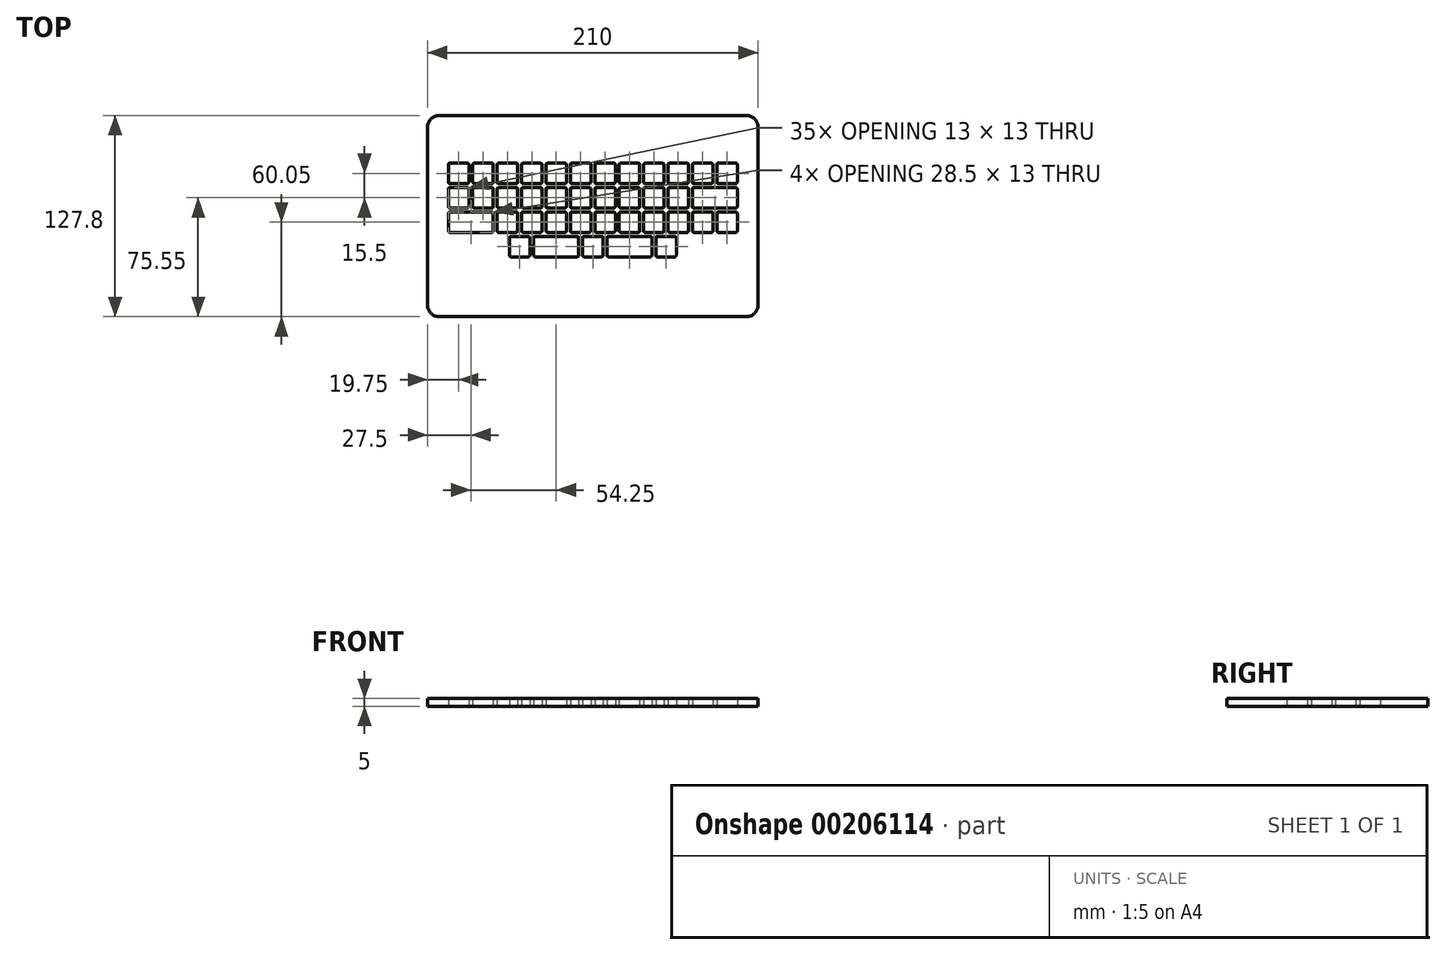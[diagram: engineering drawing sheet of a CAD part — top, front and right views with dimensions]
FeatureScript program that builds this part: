
annotation { "Feature Type Name" : "Feature", "Feature Type Description" : "" }
export const myFeature = defineFeature(function(context is Context, id is Id, definition is map)
    precondition{}
    {
        {
            var Q0;
            Q0=qCreatedBy(makeId("Top.planeOp"),FACE);
            var sketch = newSketch(context, id + "F0", { "sketchPlane" : qUnion([Q0])});
            skLineSegment(sketch, "E0.bottom", {"start": v(1, 0) * mm, "end": v(12, 0) * mm});
            skLineSegment(sketch, "E0.top", {"start": v(1, -13) * mm, "end": v(12, -13) * mm});
            skLineSegment(sketch, "E0.left", {"start": v(0, -1) * mm, "end": v(0, -12) * mm});
            skLineSegment(sketch, "E0.right", {"start": v(13, -1) * mm, "end": v(13, -12) * mm});
            skPoint(sketch, "E1.visualSharp", {"position": v(13, 0) * mm});
            skArc(sketch, "E1.filletArc", {"start": v(13, -1) * mm, "mid": v(12.7, -0.3) * mm, "end": v(12, 0) * mm});
            skArc(sketch, "E2.filletArc", {"start": v(12, -13) * mm, "mid": v(12.7, -12.7) * mm, "end": v(13, -12) * mm});
            skArc(sketch, "E3.filletArc", {"start": v(0, -12) * mm, "mid": v(0.3, -12.7) * mm, "end": v(1, -13) * mm});
            skPoint(sketch, "E4.visualSharp", {"position": v(0, 0) * mm});
            skArc(sketch, "E4.filletArc", {"start": v(1, 0) * mm, "mid": v(0.3, -0.3) * mm, "end": v(0, -1) * mm});
            skLineSegment(sketch, "E5.1.0.1", {"start": v(16.5, -13) * mm, "end": v(27.5, -13) * mm});
            skLineSegment(sketch, "E5.1.0.2", {"start": v(28.5, -1) * mm, "end": v(28.5, -12) * mm});
            skLineSegment(sketch, "E5.1.0.3", {"start": v(15.5, -1) * mm, "end": v(15.5, -12) * mm});
            skLineSegment(sketch, "E5.1.0.4", {"start": v(16.5, 0) * mm, "end": v(27.5, 0) * mm});
            skPoint(sketch, "E5.1.0.5", {"position": v(15.5, 0) * mm});
            skPoint(sketch, "E5.1.0.6", {"position": v(28.5, 0) * mm});
            skArc(sketch, "E5.1.0.8", {"start": v(28.5, -1) * mm, "mid": v(28.2, -0.3) * mm, "end": v(27.5, 0) * mm});
            skArc(sketch, "E5.1.0.9", {"start": v(27.5, -13) * mm, "mid": v(28.2, -12.7) * mm, "end": v(28.5, -12) * mm});
            skArc(sketch, "E5.1.0.10", {"start": v(15.5, -12) * mm, "mid": v(15.8, -12.7) * mm, "end": v(16.5, -13) * mm});
            skArc(sketch, "E5.1.0.11", {"start": v(16.5, 0) * mm, "mid": v(15.8, -0.3) * mm, "end": v(15.5, -1) * mm});
            skLineSegment(sketch, "E5.2.0.1", {"start": v(32, -13) * mm, "end": v(43, -13) * mm});
            skLineSegment(sketch, "E5.2.0.2", {"start": v(44, -1) * mm, "end": v(44, -12) * mm});
            skLineSegment(sketch, "E5.2.0.3", {"start": v(31, -1) * mm, "end": v(31, -12) * mm});
            skLineSegment(sketch, "E5.2.0.4", {"start": v(32, 0) * mm, "end": v(43, 0) * mm});
            skPoint(sketch, "E5.2.0.5", {"position": v(31, 0) * mm});
            skPoint(sketch, "E5.2.0.6", {"position": v(44, 0) * mm});
            skArc(sketch, "E5.2.0.8", {"start": v(44, -1) * mm, "mid": v(43.7, -0.3) * mm, "end": v(43, 0) * mm});
            skArc(sketch, "E5.2.0.9", {"start": v(43, -13) * mm, "mid": v(43.7, -12.7) * mm, "end": v(44, -12) * mm});
            skArc(sketch, "E5.2.0.10", {"start": v(31, -12) * mm, "mid": v(31.3, -12.7) * mm, "end": v(32, -13) * mm});
            skArc(sketch, "E5.2.0.11", {"start": v(32, 0) * mm, "mid": v(31.3, -0.3) * mm, "end": v(31, -1) * mm});
            skLineSegment(sketch, "E5.3.0.1", {"start": v(47.5, -13) * mm, "end": v(58.5, -13) * mm});
            skLineSegment(sketch, "E5.3.0.2", {"start": v(59.5, -1) * mm, "end": v(59.5, -12) * mm});
            skLineSegment(sketch, "E5.3.0.3", {"start": v(46.5, -1) * mm, "end": v(46.5, -12) * mm});
            skLineSegment(sketch, "E5.3.0.4", {"start": v(47.5, 0) * mm, "end": v(58.5, 0) * mm});
            skPoint(sketch, "E5.3.0.5", {"position": v(46.5, 0) * mm});
            skPoint(sketch, "E5.3.0.6", {"position": v(59.5, 0) * mm});
            skArc(sketch, "E5.3.0.8", {"start": v(59.5, -1) * mm, "mid": v(59.2, -0.3) * mm, "end": v(58.5, 0) * mm});
            skArc(sketch, "E5.3.0.9", {"start": v(58.5, -13) * mm, "mid": v(59.2, -12.7) * mm, "end": v(59.5, -12) * mm});
            skArc(sketch, "E5.3.0.10", {"start": v(46.5, -12) * mm, "mid": v(46.8, -12.7) * mm, "end": v(47.5, -13) * mm});
            skArc(sketch, "E5.3.0.11", {"start": v(47.5, 0) * mm, "mid": v(46.8, -0.3) * mm, "end": v(46.5, -1) * mm});
            skLineSegment(sketch, "E5.4.0.1", {"start": v(63, -13) * mm, "end": v(74, -13) * mm});
            skLineSegment(sketch, "E5.4.0.2", {"start": v(75, -1) * mm, "end": v(75, -12) * mm});
            skLineSegment(sketch, "E5.4.0.3", {"start": v(62, -1) * mm, "end": v(62, -12) * mm});
            skLineSegment(sketch, "E5.4.0.4", {"start": v(63, 0) * mm, "end": v(74, 0) * mm});
            skPoint(sketch, "E5.4.0.5", {"position": v(62, 0) * mm});
            skPoint(sketch, "E5.4.0.6", {"position": v(75, 0) * mm});
            skArc(sketch, "E5.4.0.8", {"start": v(75, -1) * mm, "mid": v(74.7, -0.3) * mm, "end": v(74, 0) * mm});
            skArc(sketch, "E5.4.0.9", {"start": v(74, -13) * mm, "mid": v(74.7, -12.7) * mm, "end": v(75, -12) * mm});
            skArc(sketch, "E5.4.0.10", {"start": v(62, -12) * mm, "mid": v(62.3, -12.7) * mm, "end": v(63, -13) * mm});
            skArc(sketch, "E5.4.0.11", {"start": v(63, 0) * mm, "mid": v(62.3, -0.3) * mm, "end": v(62, -1) * mm});
            skLineSegment(sketch, "E5.5.0.1", {"start": v(78.5, -13) * mm, "end": v(89.5, -13) * mm});
            skLineSegment(sketch, "E5.5.0.2", {"start": v(90.5, -1) * mm, "end": v(90.5, -12) * mm});
            skLineSegment(sketch, "E5.5.0.3", {"start": v(77.5, -1) * mm, "end": v(77.5, -12) * mm});
            skLineSegment(sketch, "E5.5.0.4", {"start": v(78.5, 0) * mm, "end": v(89.5, 0) * mm});
            skPoint(sketch, "E5.5.0.5", {"position": v(77.5, 0) * mm});
            skPoint(sketch, "E5.5.0.6", {"position": v(90.5, 0) * mm});
            skArc(sketch, "E5.5.0.8", {"start": v(90.5, -1) * mm, "mid": v(90.2, -0.3) * mm, "end": v(89.5, 0) * mm});
            skArc(sketch, "E5.5.0.9", {"start": v(89.5, -13) * mm, "mid": v(90.2, -12.7) * mm, "end": v(90.5, -12) * mm});
            skArc(sketch, "E5.5.0.10", {"start": v(77.5, -12) * mm, "mid": v(77.8, -12.7) * mm, "end": v(78.5, -13) * mm});
            skArc(sketch, "E5.5.0.11", {"start": v(78.5, 0) * mm, "mid": v(77.8, -0.3) * mm, "end": v(77.5, -1) * mm});
            skLineSegment(sketch, "E5.6.0.1", {"start": v(94, -13) * mm, "end": v(105, -13) * mm});
            skLineSegment(sketch, "E5.6.0.2", {"start": v(106, -1) * mm, "end": v(106, -12) * mm});
            skLineSegment(sketch, "E5.6.0.3", {"start": v(93, -1) * mm, "end": v(93, -12) * mm});
            skLineSegment(sketch, "E5.6.0.4", {"start": v(94, 0) * mm, "end": v(105, 0) * mm});
            skPoint(sketch, "E5.6.0.5", {"position": v(93, 0) * mm});
            skPoint(sketch, "E5.6.0.6", {"position": v(106, 0) * mm});
            skArc(sketch, "E5.6.0.8", {"start": v(106, -1) * mm, "mid": v(105.7, -0.3) * mm, "end": v(105, 0) * mm});
            skArc(sketch, "E5.6.0.9", {"start": v(105, -13) * mm, "mid": v(105.7, -12.7) * mm, "end": v(106, -12) * mm});
            skArc(sketch, "E5.6.0.10", {"start": v(93, -12) * mm, "mid": v(93.3, -12.7) * mm, "end": v(94, -13) * mm});
            skArc(sketch, "E5.6.0.11", {"start": v(94, 0) * mm, "mid": v(93.3, -0.3) * mm, "end": v(93, -1) * mm});
            skLineSegment(sketch, "E5.7.0.1", {"start": v(109.5, -13) * mm, "end": v(120.5, -13) * mm});
            skLineSegment(sketch, "E5.7.0.2", {"start": v(121.5, -1) * mm, "end": v(121.5, -12) * mm});
            skLineSegment(sketch, "E5.7.0.3", {"start": v(108.5, -1) * mm, "end": v(108.5, -12) * mm});
            skLineSegment(sketch, "E5.7.0.4", {"start": v(109.5, 0) * mm, "end": v(120.5, 0) * mm});
            skPoint(sketch, "E5.7.0.5", {"position": v(108.5, 0) * mm});
            skPoint(sketch, "E5.7.0.6", {"position": v(121.5, 0) * mm});
            skArc(sketch, "E5.7.0.8", {"start": v(121.5, -1) * mm, "mid": v(121.2, -0.3) * mm, "end": v(120.5, 0) * mm});
            skArc(sketch, "E5.7.0.9", {"start": v(120.5, -13) * mm, "mid": v(121.2, -12.7) * mm, "end": v(121.5, -12) * mm});
            skArc(sketch, "E5.7.0.10", {"start": v(108.5, -12) * mm, "mid": v(108.8, -12.7) * mm, "end": v(109.5, -13) * mm});
            skArc(sketch, "E5.7.0.11", {"start": v(109.5, 0) * mm, "mid": v(108.8, -0.3) * mm, "end": v(108.5, -1) * mm});
            skLineSegment(sketch, "E5.8.0.1", {"start": v(125, -13) * mm, "end": v(136, -13) * mm});
            skLineSegment(sketch, "E5.8.0.2", {"start": v(137, -1) * mm, "end": v(137, -12) * mm});
            skLineSegment(sketch, "E5.8.0.3", {"start": v(124, -1) * mm, "end": v(124, -12) * mm});
            skLineSegment(sketch, "E5.8.0.4", {"start": v(125, 0) * mm, "end": v(136, 0) * mm});
            skPoint(sketch, "E5.8.0.5", {"position": v(124, 0) * mm});
            skPoint(sketch, "E5.8.0.6", {"position": v(137, 0) * mm});
            skArc(sketch, "E5.8.0.8", {"start": v(137, -1) * mm, "mid": v(136.7, -0.3) * mm, "end": v(136, 0) * mm});
            skArc(sketch, "E5.8.0.9", {"start": v(136, -13) * mm, "mid": v(136.7, -12.7) * mm, "end": v(137, -12) * mm});
            skArc(sketch, "E5.8.0.10", {"start": v(124, -12) * mm, "mid": v(124.3, -12.7) * mm, "end": v(125, -13) * mm});
            skArc(sketch, "E5.8.0.11", {"start": v(125, 0) * mm, "mid": v(124.3, -0.3) * mm, "end": v(124, -1) * mm});
            skLineSegment(sketch, "E5.9.0.1", {"start": v(140.5, -13) * mm, "end": v(151.5, -13) * mm});
            skLineSegment(sketch, "E5.9.0.2", {"start": v(152.5, -1) * mm, "end": v(152.5, -12) * mm});
            skLineSegment(sketch, "E5.9.0.3", {"start": v(139.5, -1) * mm, "end": v(139.5, -12) * mm});
            skLineSegment(sketch, "E5.9.0.4", {"start": v(140.5, 0) * mm, "end": v(151.5, 0) * mm});
            skPoint(sketch, "E5.9.0.5", {"position": v(139.5, 0) * mm});
            skPoint(sketch, "E5.9.0.6", {"position": v(152.5, 0) * mm});
            skArc(sketch, "E5.9.0.8", {"start": v(152.5, -1) * mm, "mid": v(152.2, -0.3) * mm, "end": v(151.5, 0) * mm});
            skArc(sketch, "E5.9.0.9", {"start": v(151.5, -13) * mm, "mid": v(152.2, -12.7) * mm, "end": v(152.5, -12) * mm});
            skArc(sketch, "E5.9.0.10", {"start": v(139.5, -12) * mm, "mid": v(139.8, -12.7) * mm, "end": v(140.5, -13) * mm});
            skArc(sketch, "E5.9.0.11", {"start": v(140.5, 0) * mm, "mid": v(139.8, -0.3) * mm, "end": v(139.5, -1) * mm});
            skLineSegment(sketch, "E5.10.0.1", {"start": v(156, -13) * mm, "end": v(167, -13) * mm});
            skLineSegment(sketch, "E5.10.0.2", {"start": v(168, -1) * mm, "end": v(168, -12) * mm});
            skLineSegment(sketch, "E5.10.0.3", {"start": v(155, -1) * mm, "end": v(155, -12) * mm});
            skLineSegment(sketch, "E5.10.0.4", {"start": v(156, 0) * mm, "end": v(167, 0) * mm});
            skPoint(sketch, "E5.10.0.5", {"position": v(155, 0) * mm});
            skPoint(sketch, "E5.10.0.6", {"position": v(168, 0) * mm});
            skArc(sketch, "E5.10.0.8", {"start": v(168, -1) * mm, "mid": v(167.7, -0.3) * mm, "end": v(167, 0) * mm});
            skArc(sketch, "E5.10.0.9", {"start": v(167, -13) * mm, "mid": v(167.7, -12.7) * mm, "end": v(168, -12) * mm});
            skArc(sketch, "E5.10.0.10", {"start": v(155, -12) * mm, "mid": v(155.3, -12.7) * mm, "end": v(156, -13) * mm});
            skArc(sketch, "E5.10.0.11", {"start": v(156, 0) * mm, "mid": v(155.3, -0.3) * mm, "end": v(155, -1) * mm});
            skLineSegment(sketch, "E5.11.0.1", {"start": v(171.5, -13) * mm, "end": v(182.5, -13) * mm});
            skLineSegment(sketch, "E5.11.0.2", {"start": v(183.5, -1) * mm, "end": v(183.5, -12) * mm});
            skLineSegment(sketch, "E5.11.0.3", {"start": v(170.5, -1) * mm, "end": v(170.5, -12) * mm});
            skLineSegment(sketch, "E5.11.0.4", {"start": v(171.5, 0) * mm, "end": v(182.5, 0) * mm});
            skPoint(sketch, "E5.11.0.5", {"position": v(170.5, 0) * mm});
            skPoint(sketch, "E5.11.0.6", {"position": v(183.5, 0) * mm});
            skArc(sketch, "E5.11.0.8", {"start": v(183.5, -1) * mm, "mid": v(183.2, -0.3) * mm, "end": v(182.5, 0) * mm});
            skArc(sketch, "E5.11.0.9", {"start": v(182.5, -13) * mm, "mid": v(183.2, -12.7) * mm, "end": v(183.5, -12) * mm});
            skArc(sketch, "E5.11.0.10", {"start": v(170.5, -12) * mm, "mid": v(170.8, -12.7) * mm, "end": v(171.5, -13) * mm});
            skArc(sketch, "E5.11.0.11", {"start": v(171.5, 0) * mm, "mid": v(170.8, -0.3) * mm, "end": v(170.5, -1) * mm});
            skLineSegment(sketch, "E5.direction1", {"start": v(0, -13) * mm, "end": v(15.5, -13) * mm, "construction": true});
            skLineSegment(sketch, "E6.0.1.0", {"start": v(121.5, -16.5) * mm, "end": v(121.5, -27.5) * mm});
            skPoint(sketch, "E6.0.1.1", {"position": v(183.5, -15.5) * mm});
            skPoint(sketch, "E6.0.1.2", {"position": v(155, -15.5) * mm});
            skLineSegment(sketch, "E6.0.1.3", {"start": v(140.5, -15.5) * mm, "end": v(151.5, -15.5) * mm});
            skLineSegment(sketch, "E6.0.1.5", {"start": v(47.5, -15.5) * mm, "end": v(58.5, -15.5) * mm});
            skLineSegment(sketch, "E6.0.1.6", {"start": v(78.5, -15.5) * mm, "end": v(89.5, -15.5) * mm});
            skLineSegment(sketch, "E6.0.1.7", {"start": v(109.5, -15.5) * mm, "end": v(120.5, -15.5) * mm});
            skPoint(sketch, "E6.0.1.8", {"position": v(46.5, -15.5) * mm});
            skLineSegment(sketch, "E6.0.1.9", {"start": v(63, -15.5) * mm, "end": v(74, -15.5) * mm});
            skLineSegment(sketch, "E6.0.1.10", {"start": v(94, -15.5) * mm, "end": v(105, -15.5) * mm});
            skLineSegment(sketch, "E6.0.1.11", {"start": v(125, -15.5) * mm, "end": v(136, -15.5) * mm});
            skLineSegment(sketch, "E6.0.1.13", {"start": v(46.5, -16.5) * mm, "end": v(46.5, -27.5) * mm});
            skLineSegment(sketch, "E6.0.1.14", {"start": v(108.5, -16.5) * mm, "end": v(108.5, -27.5) * mm});
            skPoint(sketch, "E6.0.1.15", {"position": v(137, -15.5) * mm});
            skPoint(sketch, "E6.0.1.16", {"position": v(13, -15.5) * mm});
            skLineSegment(sketch, "E6.0.1.17", {"start": v(75, -16.5) * mm, "end": v(75, -27.5) * mm});
            skLineSegment(sketch, "E6.0.1.19", {"start": v(155, -16.5) * mm, "end": v(155, -27.5) * mm});
            skLineSegment(sketch, "E6.0.1.20", {"start": v(31, -16.5) * mm, "end": v(31, -27.5) * mm});
            skPoint(sketch, "E6.0.1.21", {"position": v(124, -15.5) * mm});
            skLineSegment(sketch, "E6.0.1.22", {"start": v(152.5, -16.5) * mm, "end": v(152.5, -27.5) * mm});
            skPoint(sketch, "E6.0.1.23", {"position": v(0, -15.5) * mm});
            skLineSegment(sketch, "E6.0.1.24", {"start": v(44, -16.5) * mm, "end": v(44, -27.5) * mm});
            skLineSegment(sketch, "E6.0.1.25", {"start": v(59.5, -16.5) * mm, "end": v(59.5, -27.5) * mm});
            skPoint(sketch, "E6.0.1.26", {"position": v(31, -15.5) * mm});
            skPoint(sketch, "E6.0.1.27", {"position": v(90.5, -15.5) * mm});
            skLineSegment(sketch, "E6.0.1.28", {"start": v(171.5, -28.5) * mm, "end": v(182.5, -28.5) * mm});
            skLineSegment(sketch, "E6.0.1.29", {"start": v(109.5, -28.5) * mm, "end": v(120.5, -28.5) * mm});
            skLineSegment(sketch, "E6.0.1.30", {"start": v(78.5, -28.5) * mm, "end": v(89.5, -28.5) * mm});
            skPoint(sketch, "E6.0.1.31", {"position": v(139.5, -15.5) * mm});
            skPoint(sketch, "E6.0.1.32", {"position": v(15.5, -15.5) * mm});
            skLineSegment(sketch, "E6.0.1.33", {"start": v(125, -28.5) * mm, "end": v(136, -28.5) * mm});
            skLineSegment(sketch, "E6.0.1.34", {"start": v(94, -28.5) * mm, "end": v(105, -28.5) * mm});
            skLineSegment(sketch, "E6.0.1.35", {"start": v(156, -28.5) * mm, "end": v(167, -28.5) * mm});
            skLineSegment(sketch, "E6.0.1.36", {"start": v(32, -28.5) * mm, "end": v(43, -28.5) * mm});
            skPoint(sketch, "E6.0.1.37", {"position": v(77.5, -15.5) * mm});
            skLineSegment(sketch, "E6.0.1.38", {"start": v(0, -28.5) * mm, "end": v(15.5, -28.5) * mm, "construction": true});
            skLineSegment(sketch, "E6.0.1.39", {"start": v(16.5, -15.5) * mm, "end": v(27.5, -15.5) * mm});
            skLineSegment(sketch, "E6.0.1.40", {"start": v(15.5, -16.5) * mm, "end": v(15.5, -27.5) * mm});
            skLineSegment(sketch, "E6.0.1.41", {"start": v(28.5, -16.5) * mm, "end": v(28.5, -27.5) * mm});
            skLineSegment(sketch, "E6.0.1.42", {"start": v(16.5, -28.5) * mm, "end": v(27.5, -28.5) * mm});
            skLineSegment(sketch, "E6.0.1.43", {"start": v(13, -16.5) * mm, "end": v(13, -27.5) * mm});
            skLineSegment(sketch, "E6.0.1.44", {"start": v(0, -16.5) * mm, "end": v(0, -27.5) * mm});
            skPoint(sketch, "E6.0.1.45", {"position": v(44, -15.5) * mm});
            skLineSegment(sketch, "E6.0.1.46", {"start": v(77.5, -16.5) * mm, "end": v(77.5, -27.5) * mm});
            skPoint(sketch, "E6.0.1.47", {"position": v(108.5, -15.5) * mm});
            skPoint(sketch, "E6.0.1.48", {"position": v(168, -15.5) * mm});
            skPoint(sketch, "E6.0.1.49", {"position": v(93, -15.5) * mm});
            skPoint(sketch, "E6.0.1.50", {"position": v(59.5, -15.5) * mm});
            skPoint(sketch, "E6.0.1.51", {"position": v(75, -15.5) * mm});
            skPoint(sketch, "E6.0.1.52", {"position": v(121.5, -15.5) * mm});
            skPoint(sketch, "E6.0.1.53", {"position": v(170.5, -15.5) * mm});
            skPoint(sketch, "E6.0.1.54", {"position": v(62, -15.5) * mm});
            skLineSegment(sketch, "E6.0.1.55", {"start": v(139.5, -16.5) * mm, "end": v(139.5, -27.5) * mm});
            skPoint(sketch, "E6.0.1.56", {"position": v(106, -15.5) * mm});
            skLineSegment(sketch, "E6.0.1.57", {"start": v(32, -15.5) * mm, "end": v(43, -15.5) * mm});
            skLineSegment(sketch, "E6.0.1.58", {"start": v(63, -28.5) * mm, "end": v(74, -28.5) * mm});
            skLineSegment(sketch, "E6.0.1.59", {"start": v(47.5, -28.5) * mm, "end": v(58.5, -28.5) * mm});
            skLineSegment(sketch, "E6.0.1.60", {"start": v(140.5, -28.5) * mm, "end": v(151.5, -28.5) * mm});
            skLineSegment(sketch, "E6.0.1.61", {"start": v(137, -16.5) * mm, "end": v(137, -27.5) * mm});
            skLineSegment(sketch, "E6.0.1.62", {"start": v(106, -16.5) * mm, "end": v(106, -27.5) * mm});
            skPoint(sketch, "E6.0.1.64", {"position": v(152.5, -15.5) * mm});
            skLineSegment(sketch, "E6.0.1.65", {"start": v(90.5, -16.5) * mm, "end": v(90.5, -27.5) * mm});
            skLineSegment(sketch, "E6.0.1.66", {"start": v(183.5, -16.5) * mm, "end": v(183.5, -27.5) * mm});
            skLineSegment(sketch, "E6.0.1.67", {"start": v(124, -16.5) * mm, "end": v(124, -27.5) * mm});
            skLineSegment(sketch, "E6.0.1.68", {"start": v(93, -16.5) * mm, "end": v(93, -27.5) * mm});
            skLineSegment(sketch, "E6.0.1.69", {"start": v(62, -16.5) * mm, "end": v(62, -27.5) * mm});
            skPoint(sketch, "E6.0.1.70", {"position": v(28.5, -15.5) * mm});
            skLineSegment(sketch, "E6.0.1.71", {"start": v(1, -15.5) * mm, "end": v(12, -15.5) * mm});
            skLineSegment(sketch, "E6.0.1.72", {"start": v(1, -28.5) * mm, "end": v(12, -28.5) * mm});
            skArc(sketch, "E6.0.1.73", {"start": v(182.5, -28.5) * mm, "mid": v(183.2, -28.2) * mm, "end": v(183.5, -27.5) * mm});
            skArc(sketch, "E6.0.1.74", {"start": v(89.5, -28.5) * mm, "mid": v(90.2, -28.2) * mm, "end": v(90.5, -27.5) * mm});
            skArc(sketch, "E6.0.1.75", {"start": v(31, -27.5) * mm, "mid": v(31.3, -28.2) * mm, "end": v(32, -28.5) * mm});
            skArc(sketch, "E6.0.1.76", {"start": v(74, -28.5) * mm, "mid": v(74.7, -28.2) * mm, "end": v(75, -27.5) * mm});
            skArc(sketch, "E6.0.1.77", {"start": v(155, -27.5) * mm, "mid": v(155.3, -28.2) * mm, "end": v(156, -28.5) * mm});
            skArc(sketch, "E6.0.1.78", {"start": v(77.5, -27.5) * mm, "mid": v(77.8, -28.2) * mm, "end": v(78.5, -28.5) * mm});
            skArc(sketch, "E6.0.1.79", {"start": v(139.5, -27.5) * mm, "mid": v(139.8, -28.2) * mm, "end": v(140.5, -28.5) * mm});
            skArc(sketch, "E6.0.1.80", {"start": v(93, -27.5) * mm, "mid": v(93.3, -28.2) * mm, "end": v(94, -28.5) * mm});
            skArc(sketch, "E6.0.1.81", {"start": v(62, -27.5) * mm, "mid": v(62.3, -28.2) * mm, "end": v(63, -28.5) * mm});
            skArc(sketch, "E6.0.1.82", {"start": v(75, -16.5) * mm, "mid": v(74.7, -15.8) * mm, "end": v(74, -15.5) * mm});
            skArc(sketch, "E6.0.1.83", {"start": v(44, -16.5) * mm, "mid": v(43.7, -15.8) * mm, "end": v(43, -15.5) * mm});
            skArc(sketch, "E6.0.1.84", {"start": v(32, -15.5) * mm, "mid": v(31.3, -15.8) * mm, "end": v(31, -16.5) * mm});
            skArc(sketch, "E6.0.1.85", {"start": v(1, -15.5) * mm, "mid": v(0.3, -15.8) * mm, "end": v(0, -16.5) * mm});
            skArc(sketch, "E6.0.1.86", {"start": v(0, -27.5) * mm, "mid": v(0.3, -28.2) * mm, "end": v(1, -28.5) * mm});
            skArc(sketch, "E6.0.1.87", {"start": v(12, -28.5) * mm, "mid": v(12.7, -28.2) * mm, "end": v(13, -27.5) * mm});
            skArc(sketch, "E6.0.1.88", {"start": v(13, -16.5) * mm, "mid": v(12.7, -15.8) * mm, "end": v(12, -15.5) * mm});
            skArc(sketch, "E6.0.1.89", {"start": v(27.5, -28.5) * mm, "mid": v(28.2, -28.2) * mm, "end": v(28.5, -27.5) * mm});
            skArc(sketch, "E6.0.1.90", {"start": v(140.5, -15.5) * mm, "mid": v(139.8, -15.8) * mm, "end": v(139.5, -16.5) * mm});
            skArc(sketch, "E6.0.1.92", {"start": v(46.5, -27.5) * mm, "mid": v(46.8, -28.2) * mm, "end": v(47.5, -28.5) * mm});
            skArc(sketch, "E6.0.1.93", {"start": v(105, -28.5) * mm, "mid": v(105.7, -28.2) * mm, "end": v(106, -27.5) * mm});
            skArc(sketch, "E6.0.1.94", {"start": v(108.5, -27.5) * mm, "mid": v(108.8, -28.2) * mm, "end": v(109.5, -28.5) * mm});
            skArc(sketch, "E6.0.1.95", {"start": v(136, -28.5) * mm, "mid": v(136.7, -28.2) * mm, "end": v(137, -27.5) * mm});
            skArc(sketch, "E6.0.1.97", {"start": v(124, -27.5) * mm, "mid": v(124.3, -28.2) * mm, "end": v(125, -28.5) * mm});
            skArc(sketch, "E6.0.1.98", {"start": v(43, -28.5) * mm, "mid": v(43.7, -28.2) * mm, "end": v(44, -27.5) * mm});
            skArc(sketch, "E6.0.1.99", {"start": v(152.5, -16.5) * mm, "mid": v(152.2, -15.8) * mm, "end": v(151.5, -15.5) * mm});
            skArc(sketch, "E6.0.1.100", {"start": v(183.5, -16.5) * mm, "mid": v(183.2, -15.8) * mm, "end": v(182.5, -15.5) * mm});
            skArc(sketch, "E6.0.1.101", {"start": v(59.5, -16.5) * mm, "mid": v(59.2, -15.8) * mm, "end": v(58.5, -15.5) * mm});
            skArc(sketch, "E6.0.1.102", {"start": v(90.5, -16.5) * mm, "mid": v(90.2, -15.8) * mm, "end": v(89.5, -15.5) * mm});
            skArc(sketch, "E6.0.1.103", {"start": v(121.5, -16.5) * mm, "mid": v(121.2, -15.8) * mm, "end": v(120.5, -15.5) * mm});
            skArc(sketch, "E6.0.1.104", {"start": v(58.5, -28.5) * mm, "mid": v(59.2, -28.2) * mm, "end": v(59.5, -27.5) * mm});
            skArc(sketch, "E6.0.1.105", {"start": v(106, -16.5) * mm, "mid": v(105.7, -15.8) * mm, "end": v(105, -15.5) * mm});
            skArc(sketch, "E6.0.1.106", {"start": v(120.5, -28.5) * mm, "mid": v(121.2, -28.2) * mm, "end": v(121.5, -27.5) * mm});
            skArc(sketch, "E6.0.1.107", {"start": v(137, -16.5) * mm, "mid": v(136.7, -15.8) * mm, "end": v(136, -15.5) * mm});
            skArc(sketch, "E6.0.1.108", {"start": v(151.5, -28.5) * mm, "mid": v(152.2, -28.2) * mm, "end": v(152.5, -27.5) * mm});
            skArc(sketch, "E6.0.1.110", {"start": v(78.5, -15.5) * mm, "mid": v(77.8, -15.8) * mm, "end": v(77.5, -16.5) * mm});
            skArc(sketch, "E6.0.1.111", {"start": v(15.5, -27.5) * mm, "mid": v(15.8, -28.2) * mm, "end": v(16.5, -28.5) * mm});
            skArc(sketch, "E6.0.1.112", {"start": v(16.5, -15.5) * mm, "mid": v(15.8, -15.8) * mm, "end": v(15.5, -16.5) * mm});
            skArc(sketch, "E6.0.1.113", {"start": v(28.5, -16.5) * mm, "mid": v(28.2, -15.8) * mm, "end": v(27.5, -15.5) * mm});
            skArc(sketch, "E6.0.1.114", {"start": v(94, -15.5) * mm, "mid": v(93.3, -15.8) * mm, "end": v(93, -16.5) * mm});
            skArc(sketch, "E6.0.1.115", {"start": v(156, -15.5) * mm, "mid": v(155.3, -15.8) * mm, "end": v(155, -16.5) * mm});
            skArc(sketch, "E6.0.1.117", {"start": v(47.5, -15.5) * mm, "mid": v(46.8, -15.8) * mm, "end": v(46.5, -16.5) * mm});
            skArc(sketch, "E6.0.1.118", {"start": v(109.5, -15.5) * mm, "mid": v(108.8, -15.8) * mm, "end": v(108.5, -16.5) * mm});
            skArc(sketch, "E6.0.1.119", {"start": v(63, -15.5) * mm, "mid": v(62.3, -15.8) * mm, "end": v(62, -16.5) * mm});
            skArc(sketch, "E6.0.1.120", {"start": v(125, -15.5) * mm, "mid": v(124.3, -15.8) * mm, "end": v(124, -16.5) * mm});
            skLineSegment(sketch, "E6.0.2.0", {"start": v(121.5, -32) * mm, "end": v(121.5, -43) * mm});
            skPoint(sketch, "E6.0.2.1", {"position": v(183.5, -31) * mm});
            skPoint(sketch, "E6.0.2.2", {"position": v(155, -31) * mm});
            skLineSegment(sketch, "E6.0.2.3", {"start": v(140.5, -31) * mm, "end": v(151.5, -31) * mm});
            skLineSegment(sketch, "E6.0.2.4", {"start": v(171.5, -31) * mm, "end": v(182.5, -31) * mm});
            skLineSegment(sketch, "E6.0.2.5", {"start": v(47.5, -31) * mm, "end": v(58.5, -31) * mm});
            skLineSegment(sketch, "E6.0.2.6", {"start": v(78.5, -31) * mm, "end": v(89.5, -31) * mm});
            skLineSegment(sketch, "E6.0.2.7", {"start": v(109.5, -31) * mm, "end": v(120.5, -31) * mm});
            skPoint(sketch, "E6.0.2.8", {"position": v(46.5, -31) * mm});
            skLineSegment(sketch, "E6.0.2.9", {"start": v(63, -31) * mm, "end": v(74, -31) * mm});
            skLineSegment(sketch, "E6.0.2.10", {"start": v(94, -31) * mm, "end": v(105, -31) * mm});
            skLineSegment(sketch, "E6.0.2.11", {"start": v(125, -31) * mm, "end": v(136, -31) * mm});
            skLineSegment(sketch, "E6.0.2.12", {"start": v(170.5, -32) * mm, "end": v(170.5, -43) * mm});
            skLineSegment(sketch, "E6.0.2.13", {"start": v(46.5, -32) * mm, "end": v(46.5, -43) * mm});
            skLineSegment(sketch, "E6.0.2.14", {"start": v(108.5, -32) * mm, "end": v(108.5, -43) * mm});
            skPoint(sketch, "E6.0.2.15", {"position": v(137, -31) * mm});
            skPoint(sketch, "E6.0.2.16", {"position": v(13, -31) * mm});
            skLineSegment(sketch, "E6.0.2.17", {"start": v(75, -32) * mm, "end": v(75, -43) * mm});
            skLineSegment(sketch, "E6.0.2.18", {"start": v(168, -32) * mm, "end": v(168, -43) * mm});
            skLineSegment(sketch, "E6.0.2.19", {"start": v(155, -32) * mm, "end": v(155, -43) * mm});
            skLineSegment(sketch, "E6.0.2.20", {"start": v(31, -32) * mm, "end": v(31, -43) * mm});
            skPoint(sketch, "E6.0.2.21", {"position": v(124, -31) * mm});
            skLineSegment(sketch, "E6.0.2.22", {"start": v(152.5, -32) * mm, "end": v(152.5, -43) * mm});
            skPoint(sketch, "E6.0.2.23", {"position": v(0, -31) * mm});
            skLineSegment(sketch, "E6.0.2.24", {"start": v(44, -32) * mm, "end": v(44, -43) * mm});
            skLineSegment(sketch, "E6.0.2.25", {"start": v(59.5, -32) * mm, "end": v(59.5, -43) * mm});
            skPoint(sketch, "E6.0.2.26", {"position": v(31, -31) * mm});
            skPoint(sketch, "E6.0.2.27", {"position": v(90.5, -31) * mm});
            skLineSegment(sketch, "E6.0.2.28", {"start": v(171.5, -44) * mm, "end": v(182.5, -44) * mm});
            skLineSegment(sketch, "E6.0.2.29", {"start": v(109.5, -44) * mm, "end": v(120.5, -44) * mm});
            skLineSegment(sketch, "E6.0.2.30", {"start": v(78.5, -44) * mm, "end": v(89.5, -44) * mm});
            skPoint(sketch, "E6.0.2.31", {"position": v(139.5, -31) * mm});
            skPoint(sketch, "E6.0.2.32", {"position": v(15.5, -31) * mm});
            skLineSegment(sketch, "E6.0.2.33", {"start": v(125, -44) * mm, "end": v(136, -44) * mm});
            skLineSegment(sketch, "E6.0.2.34", {"start": v(94, -44) * mm, "end": v(105, -44) * mm});
            skLineSegment(sketch, "E6.0.2.35", {"start": v(156, -44) * mm, "end": v(167, -44) * mm});
            skLineSegment(sketch, "E6.0.2.36", {"start": v(32, -44) * mm, "end": v(43, -44) * mm});
            skPoint(sketch, "E6.0.2.37", {"position": v(77.5, -31) * mm});
            skLineSegment(sketch, "E6.0.2.38", {"start": v(0, -44) * mm, "end": v(15.5, -44) * mm, "construction": true});
            skLineSegment(sketch, "E6.0.2.39", {"start": v(16.5, -31) * mm, "end": v(27.5, -31) * mm});
            skLineSegment(sketch, "E6.0.2.41", {"start": v(28.5, -32) * mm, "end": v(28.5, -43) * mm});
            skLineSegment(sketch, "E6.0.2.42", {"start": v(16.5, -44) * mm, "end": v(27.5, -44) * mm});
            skLineSegment(sketch, "E6.0.2.44", {"start": v(0, -32) * mm, "end": v(0, -43) * mm});
            skPoint(sketch, "E6.0.2.45", {"position": v(44, -31) * mm});
            skLineSegment(sketch, "E6.0.2.46", {"start": v(77.5, -32) * mm, "end": v(77.5, -43) * mm});
            skPoint(sketch, "E6.0.2.47", {"position": v(108.5, -31) * mm});
            skPoint(sketch, "E6.0.2.48", {"position": v(168, -31) * mm});
            skPoint(sketch, "E6.0.2.49", {"position": v(93, -31) * mm});
            skPoint(sketch, "E6.0.2.50", {"position": v(59.5, -31) * mm});
            skPoint(sketch, "E6.0.2.51", {"position": v(75, -31) * mm});
            skPoint(sketch, "E6.0.2.52", {"position": v(121.5, -31) * mm});
            skPoint(sketch, "E6.0.2.53", {"position": v(170.5, -31) * mm});
            skPoint(sketch, "E6.0.2.54", {"position": v(62, -31) * mm});
            skLineSegment(sketch, "E6.0.2.55", {"start": v(139.5, -32) * mm, "end": v(139.5, -43) * mm});
            skPoint(sketch, "E6.0.2.56", {"position": v(106, -31) * mm});
            skLineSegment(sketch, "E6.0.2.57", {"start": v(32, -31) * mm, "end": v(43, -31) * mm});
            skLineSegment(sketch, "E6.0.2.58", {"start": v(63, -44) * mm, "end": v(74, -44) * mm});
            skLineSegment(sketch, "E6.0.2.59", {"start": v(47.5, -44) * mm, "end": v(58.5, -44) * mm});
            skLineSegment(sketch, "E6.0.2.60", {"start": v(140.5, -44) * mm, "end": v(151.5, -44) * mm});
            skLineSegment(sketch, "E6.0.2.61", {"start": v(137, -32) * mm, "end": v(137, -43) * mm});
            skLineSegment(sketch, "E6.0.2.62", {"start": v(106, -32) * mm, "end": v(106, -43) * mm});
            skLineSegment(sketch, "E6.0.2.63", {"start": v(156, -31) * mm, "end": v(167, -31) * mm});
            skPoint(sketch, "E6.0.2.64", {"position": v(152.5, -31) * mm});
            skLineSegment(sketch, "E6.0.2.65", {"start": v(90.5, -32) * mm, "end": v(90.5, -43) * mm});
            skLineSegment(sketch, "E6.0.2.66", {"start": v(183.5, -32) * mm, "end": v(183.5, -43) * mm});
            skLineSegment(sketch, "E6.0.2.67", {"start": v(124, -32) * mm, "end": v(124, -43) * mm});
            skLineSegment(sketch, "E6.0.2.68", {"start": v(93, -32) * mm, "end": v(93, -43) * mm});
            skLineSegment(sketch, "E6.0.2.69", {"start": v(62, -32) * mm, "end": v(62, -43) * mm});
            skPoint(sketch, "E6.0.2.70", {"position": v(28.5, -31) * mm});
            skLineSegment(sketch, "E6.0.2.71", {"start": v(1, -31) * mm, "end": v(12, -31) * mm});
            skLineSegment(sketch, "E6.0.2.72", {"start": v(1, -44) * mm, "end": v(12, -44) * mm});
            skArc(sketch, "E6.0.2.73", {"start": v(182.5, -44) * mm, "mid": v(183.2, -43.7) * mm, "end": v(183.5, -43) * mm});
            skArc(sketch, "E6.0.2.74", {"start": v(89.5, -44) * mm, "mid": v(90.2, -43.7) * mm, "end": v(90.5, -43) * mm});
            skArc(sketch, "E6.0.2.75", {"start": v(31, -43) * mm, "mid": v(31.3, -43.7) * mm, "end": v(32, -44) * mm});
            skArc(sketch, "E6.0.2.76", {"start": v(74, -44) * mm, "mid": v(74.7, -43.7) * mm, "end": v(75, -43) * mm});
            skArc(sketch, "E6.0.2.77", {"start": v(155, -43) * mm, "mid": v(155.3, -43.7) * mm, "end": v(156, -44) * mm});
            skArc(sketch, "E6.0.2.78", {"start": v(77.5, -43) * mm, "mid": v(77.8, -43.7) * mm, "end": v(78.5, -44) * mm});
            skArc(sketch, "E6.0.2.79", {"start": v(139.5, -43) * mm, "mid": v(139.8, -43.7) * mm, "end": v(140.5, -44) * mm});
            skArc(sketch, "E6.0.2.80", {"start": v(93, -43) * mm, "mid": v(93.3, -43.7) * mm, "end": v(94, -44) * mm});
            skArc(sketch, "E6.0.2.81", {"start": v(62, -43) * mm, "mid": v(62.3, -43.7) * mm, "end": v(63, -44) * mm});
            skArc(sketch, "E6.0.2.82", {"start": v(75, -32) * mm, "mid": v(74.7, -31.3) * mm, "end": v(74, -31) * mm});
            skArc(sketch, "E6.0.2.83", {"start": v(44, -32) * mm, "mid": v(43.7, -31.3) * mm, "end": v(43, -31) * mm});
            skArc(sketch, "E6.0.2.84", {"start": v(32, -31) * mm, "mid": v(31.3, -31.3) * mm, "end": v(31, -32) * mm});
            skArc(sketch, "E6.0.2.85", {"start": v(1, -31) * mm, "mid": v(0.3, -31.3) * mm, "end": v(0, -32) * mm});
            skArc(sketch, "E6.0.2.86", {"start": v(0, -43) * mm, "mid": v(0.3, -43.7) * mm, "end": v(1, -44) * mm});
            skArc(sketch, "E6.0.2.89", {"start": v(27.5, -44) * mm, "mid": v(28.2, -43.7) * mm, "end": v(28.5, -43) * mm});
            skArc(sketch, "E6.0.2.90", {"start": v(140.5, -31) * mm, "mid": v(139.8, -31.3) * mm, "end": v(139.5, -32) * mm});
            skArc(sketch, "E6.0.2.91", {"start": v(170.5, -43) * mm, "mid": v(170.8, -43.7) * mm, "end": v(171.5, -44) * mm});
            skArc(sketch, "E6.0.2.92", {"start": v(46.5, -43) * mm, "mid": v(46.8, -43.7) * mm, "end": v(47.5, -44) * mm});
            skArc(sketch, "E6.0.2.93", {"start": v(105, -44) * mm, "mid": v(105.7, -43.7) * mm, "end": v(106, -43) * mm});
            skArc(sketch, "E6.0.2.94", {"start": v(108.5, -43) * mm, "mid": v(108.8, -43.7) * mm, "end": v(109.5, -44) * mm});
            skArc(sketch, "E6.0.2.95", {"start": v(136, -44) * mm, "mid": v(136.7, -43.7) * mm, "end": v(137, -43) * mm});
            skArc(sketch, "E6.0.2.96", {"start": v(167, -44) * mm, "mid": v(167.7, -43.7) * mm, "end": v(168, -43) * mm});
            skArc(sketch, "E6.0.2.97", {"start": v(124, -43) * mm, "mid": v(124.3, -43.7) * mm, "end": v(125, -44) * mm});
            skArc(sketch, "E6.0.2.98", {"start": v(43, -44) * mm, "mid": v(43.7, -43.7) * mm, "end": v(44, -43) * mm});
            skArc(sketch, "E6.0.2.99", {"start": v(152.5, -32) * mm, "mid": v(152.2, -31.3) * mm, "end": v(151.5, -31) * mm});
            skArc(sketch, "E6.0.2.100", {"start": v(183.5, -32) * mm, "mid": v(183.2, -31.3) * mm, "end": v(182.5, -31) * mm});
            skArc(sketch, "E6.0.2.101", {"start": v(59.5, -32) * mm, "mid": v(59.2, -31.3) * mm, "end": v(58.5, -31) * mm});
            skArc(sketch, "E6.0.2.102", {"start": v(90.5, -32) * mm, "mid": v(90.2, -31.3) * mm, "end": v(89.5, -31) * mm});
            skArc(sketch, "E6.0.2.103", {"start": v(121.5, -32) * mm, "mid": v(121.2, -31.3) * mm, "end": v(120.5, -31) * mm});
            skArc(sketch, "E6.0.2.104", {"start": v(58.5, -44) * mm, "mid": v(59.2, -43.7) * mm, "end": v(59.5, -43) * mm});
            skArc(sketch, "E6.0.2.105", {"start": v(106, -32) * mm, "mid": v(105.7, -31.3) * mm, "end": v(105, -31) * mm});
            skArc(sketch, "E6.0.2.106", {"start": v(120.5, -44) * mm, "mid": v(121.2, -43.7) * mm, "end": v(121.5, -43) * mm});
            skArc(sketch, "E6.0.2.107", {"start": v(137, -32) * mm, "mid": v(136.7, -31.3) * mm, "end": v(136, -31) * mm});
            skArc(sketch, "E6.0.2.108", {"start": v(151.5, -44) * mm, "mid": v(152.2, -43.7) * mm, "end": v(152.5, -43) * mm});
            skArc(sketch, "E6.0.2.109", {"start": v(168, -32) * mm, "mid": v(167.7, -31.3) * mm, "end": v(167, -31) * mm});
            skArc(sketch, "E6.0.2.110", {"start": v(78.5, -31) * mm, "mid": v(77.8, -31.3) * mm, "end": v(77.5, -32) * mm});
            skArc(sketch, "E6.0.2.113", {"start": v(28.5, -32) * mm, "mid": v(28.2, -31.3) * mm, "end": v(27.5, -31) * mm});
            skArc(sketch, "E6.0.2.114", {"start": v(94, -31) * mm, "mid": v(93.3, -31.3) * mm, "end": v(93, -32) * mm});
            skArc(sketch, "E6.0.2.115", {"start": v(156, -31) * mm, "mid": v(155.3, -31.3) * mm, "end": v(155, -32) * mm});
            skArc(sketch, "E6.0.2.116", {"start": v(171.5, -31) * mm, "mid": v(170.8, -31.3) * mm, "end": v(170.5, -32) * mm});
            skArc(sketch, "E6.0.2.117", {"start": v(47.5, -31) * mm, "mid": v(46.8, -31.3) * mm, "end": v(46.5, -32) * mm});
            skArc(sketch, "E6.0.2.118", {"start": v(109.5, -31) * mm, "mid": v(108.8, -31.3) * mm, "end": v(108.5, -32) * mm});
            skArc(sketch, "E6.0.2.119", {"start": v(63, -31) * mm, "mid": v(62.3, -31.3) * mm, "end": v(62, -32) * mm});
            skArc(sketch, "E6.0.2.120", {"start": v(125, -31) * mm, "mid": v(124.3, -31.3) * mm, "end": v(124, -32) * mm});
            skLineSegment(sketch, "E6.direction1", {"start": v(0, -13) * mm, "end": v(25, -13) * mm, "construction": true});
            skLineSegment(sketch, "E6.direction2", {"start": v(0, -13) * mm, "end": v(0, -28.5) * mm, "construction": true});
            skLineSegment(sketch, "E7", {"start": v(167, -28.5) * mm, "end": v(171.5, -28.5) * mm});
            skLineSegment(sketch, "E8", {"start": v(12, -31) * mm, "end": v(16.5, -31) * mm});
            skLineSegment(sketch, "E9", {"start": v(12, -44) * mm, "end": v(16.5, -44) * mm});
            skLineSegment(sketch, "E10", {"start": v(89.5, -44) * mm, "end": v(94, -44) * mm});
            skLineSegment(sketch, "E11", {"start": v(91.75, -44) * mm, "end": v(91.75, -46.5) * mm});
            skLineSegment(sketch, "E12", {"start": v(91.75, -46.5) * mm, "end": v(91.75, -59.5) * mm});
            skLineSegment(sketch, "E13.bottom", {"start": v(86.25, -46.5) * mm, "end": v(97.25, -46.5) * mm});
            skLineSegment(sketch, "E13.top", {"start": v(86.25, -59.5) * mm, "end": v(97.25, -59.5) * mm});
            skLineSegment(sketch, "E13.left", {"start": v(85.25, -47.5) * mm, "end": v(85.25, -58.5) * mm});
            skLineSegment(sketch, "E13.right", {"start": v(98.25, -47.5) * mm, "end": v(98.25, -58.5) * mm});
            skPoint(sketch, "E13.middle", {"position": v(91.75, -53) * mm});
            skPoint(sketch, "E14.visualSharp", {"position": v(85.25, -46.5) * mm});
            skArc(sketch, "E14.filletArc", {"start": v(86.25, -46.5) * mm, "mid": v(85.54, -46.8) * mm, "end": v(85.25, -47.5) * mm});
            skPoint(sketch, "E15.visualSharp", {"position": v(85.25, -59.5) * mm});
            skArc(sketch, "E15.filletArc", {"start": v(85.25, -58.5) * mm, "mid": v(85.54, -59.2) * mm, "end": v(86.25, -59.5) * mm});
            skPoint(sketch, "E16.visualSharp", {"position": v(98.25, -46.5) * mm});
            skArc(sketch, "E16.filletArc", {"start": v(98.25, -47.5) * mm, "mid": v(97.96, -46.8) * mm, "end": v(97.25, -46.5) * mm});
            skPoint(sketch, "E17.visualSharp", {"position": v(98.25, -59.5) * mm});
            skArc(sketch, "E17.filletArc", {"start": v(97.25, -59.5) * mm, "mid": v(97.96, -59.2) * mm, "end": v(98.25, -58.5) * mm});
            skLineSegment(sketch, "E18", {"start": v(98.25, -46.5) * mm, "end": v(100.75, -46.5) * mm});
            skLineSegment(sketch, "E19.bottom", {"start": v(101.75, -46.5) * mm, "end": v(128.25, -46.5) * mm});
            skLineSegment(sketch, "E19.top", {"start": v(101.75, -59.5) * mm, "end": v(128.25, -59.5) * mm});
            skLineSegment(sketch, "E19.left", {"start": v(100.75, -47.5) * mm, "end": v(100.75, -58.5) * mm});
            skLineSegment(sketch, "E19.right", {"start": v(129.25, -47.5) * mm, "end": v(129.25, -58.5) * mm});
            skLineSegment(sketch, "E20", {"start": v(156, -15.5) * mm, "end": v(182.5, -15.5) * mm});
            skPoint(sketch, "E21.visualSharp", {"position": v(100.75, -46.5) * mm});
            skArc(sketch, "E21.filletArc", {"start": v(101.75, -46.5) * mm, "mid": v(101.04, -46.8) * mm, "end": v(100.75, -47.5) * mm});
            skPoint(sketch, "E22.visualSharp", {"position": v(100.75, -59.5) * mm});
            skArc(sketch, "E22.filletArc", {"start": v(100.75, -58.5) * mm, "mid": v(101.04, -59.2) * mm, "end": v(101.75, -59.5) * mm});
            skPoint(sketch, "E23.visualSharp", {"position": v(129.25, -46.5) * mm});
            skArc(sketch, "E23.filletArc", {"start": v(129.25, -47.5) * mm, "mid": v(128.96, -46.8) * mm, "end": v(128.25, -46.5) * mm});
            skPoint(sketch, "E24.visualSharp", {"position": v(129.25, -59.5) * mm});
            skArc(sketch, "E24.filletArc", {"start": v(128.25, -59.5) * mm, "mid": v(128.96, -59.2) * mm, "end": v(129.25, -58.5) * mm});
            skLineSegment(sketch, "E25", {"start": v(129.25, -46.5) * mm, "end": v(131.75, -46.5) * mm});
            skLineSegment(sketch, "E26.bottom", {"start": v(132.75, -46.5) * mm, "end": v(143.75, -46.5) * mm});
            skLineSegment(sketch, "E26.top", {"start": v(132.75, -59.5) * mm, "end": v(143.75, -59.5) * mm});
            skLineSegment(sketch, "E26.left", {"start": v(131.75, -47.5) * mm, "end": v(131.75, -58.5) * mm});
            skLineSegment(sketch, "E26.right", {"start": v(144.75, -47.5) * mm, "end": v(144.75, -58.5) * mm});
            skPoint(sketch, "E27.visualSharp", {"position": v(131.75, -46.5) * mm});
            skArc(sketch, "E27.filletArc", {"start": v(132.75, -46.5) * mm, "mid": v(132.04, -46.8) * mm, "end": v(131.75, -47.5) * mm});
            skPoint(sketch, "E28.visualSharp", {"position": v(131.75, -59.5) * mm});
            skArc(sketch, "E28.filletArc", {"start": v(131.75, -58.5) * mm, "mid": v(132.04, -59.2) * mm, "end": v(132.75, -59.5) * mm});
            skPoint(sketch, "E29.visualSharp", {"position": v(144.75, -46.5) * mm});
            skArc(sketch, "E29.filletArc", {"start": v(144.75, -47.5) * mm, "mid": v(144.46, -46.8) * mm, "end": v(143.75, -46.5) * mm});
            skPoint(sketch, "E30.visualSharp", {"position": v(144.75, -59.5) * mm});
            skArc(sketch, "E30.filletArc", {"start": v(143.75, -59.5) * mm, "mid": v(144.46, -59.2) * mm, "end": v(144.75, -58.5) * mm});
            skArc(sketch, "E31.MirrorCS", {"start": v(137, -43) * mm, "mid": v(136.7, -43.7) * mm, "end": v(136, -44) * mm});
            skArc(sketch, "E32.MirrorCS", {"start": v(55.25, -59.5) * mm, "mid": v(54.54, -59.2) * mm, "end": v(54.25, -58.5) * mm});
            skArc(sketch, "E33.MirrorCS", {"start": v(54.25, -47.5) * mm, "mid": v(54.54, -46.8) * mm, "end": v(55.25, -46.5) * mm});
            skArc(sketch, "E34.MirrorCS", {"start": v(81.75, -46.5) * mm, "mid": v(82.46, -46.8) * mm, "end": v(82.75, -47.5) * mm});
            skArc(sketch, "E35.MirrorCS", {"start": v(39.75, -59.5) * mm, "mid": v(39.04, -59.2) * mm, "end": v(38.75, -58.5) * mm});
            skArc(sketch, "E36.MirrorCS", {"start": v(82.75, -58.5) * mm, "mid": v(82.46, -59.2) * mm, "end": v(81.75, -59.5) * mm});
            skArc(sketch, "E37.MirrorCS", {"start": v(38.75, -47.5) * mm, "mid": v(39.04, -46.8) * mm, "end": v(39.75, -46.5) * mm});
            skArc(sketch, "E38.MirrorCS", {"start": v(50.75, -46.5) * mm, "mid": v(51.46, -46.8) * mm, "end": v(51.75, -47.5) * mm});
            skArc(sketch, "E39.MirrorCS", {"start": v(51.75, -58.5) * mm, "mid": v(51.46, -59.2) * mm, "end": v(50.75, -59.5) * mm});
            skLineSegment(sketch, "E40.MirrorCS", {"start": v(85.25, -46.5) * mm, "end": v(82.75, -46.5) * mm});
            skLineSegment(sketch, "E41.MirrorCS", {"start": v(54.25, -46.5) * mm, "end": v(51.75, -46.5) * mm});
            skPoint(sketch, "E42.MirrorP", {"position": v(82.75, -59.5) * mm});
            skPoint(sketch, "E43.MirrorP", {"position": v(54.25, -46.5) * mm});
            skLineSegment(sketch, "E44.MirrorCS", {"start": v(50.75, -46.5) * mm, "end": v(39.75, -46.5) * mm});
            skPoint(sketch, "E45.MirrorP", {"position": v(54.25, -59.5) * mm});
            skLineSegment(sketch, "E46.MirrorCS", {"start": v(50.75, -59.5) * mm, "end": v(39.75, -59.5) * mm});
            skLineSegment(sketch, "E47.MirrorCS", {"start": v(51.75, -47.5) * mm, "end": v(51.75, -58.5) * mm});
            skLineSegment(sketch, "E48.MirrorCS", {"start": v(81.75, -59.5) * mm, "end": v(55.25, -59.5) * mm});
            skLineSegment(sketch, "E49.MirrorCS", {"start": v(38.75, -47.5) * mm, "end": v(38.75, -58.5) * mm});
            skPoint(sketch, "E50.MirrorP", {"position": v(51.75, -46.5) * mm});
            skPoint(sketch, "E51.MirrorP", {"position": v(38.75, -46.5) * mm});
            skPoint(sketch, "E52.MirrorP", {"position": v(82.75, -46.5) * mm});
            skLineSegment(sketch, "E53.MirrorCS", {"start": v(81.75, -46.5) * mm, "end": v(55.25, -46.5) * mm});
            skLineSegment(sketch, "E54.MirrorCS", {"start": v(82.75, -47.5) * mm, "end": v(82.75, -58.5) * mm});
            skPoint(sketch, "E55.MirrorP", {"position": v(51.75, -59.5) * mm});
            skPoint(sketch, "E56.MirrorP", {"position": v(38.75, -59.5) * mm});
            skLineSegment(sketch, "E57.MirrorCS", {"start": v(54.25, -47.5) * mm, "end": v(54.25, -58.5) * mm});
            skLineSegment(sketch, "E58", {"start": v(89.5, -32) * mm, "end": v(94, -27.5) * mm});
            skLineSegment(sketch, "E59", {"start": v(89.5, -27.5) * mm, "end": v(91.75, -29.75) * mm});
            skLineSegment(sketch, "E60.bottom", {"start": v(189.25, 30.25) * mm, "end": v(-5.75, 30.25) * mm});
            skLineSegment(sketch, "E60.top", {"start": v(189.25, -89.75) * mm, "end": v(-5.75, -89.75) * mm});
            skLineSegment(sketch, "E60.left", {"start": v(196.75, 22.75) * mm, "end": v(196.75, -82.25) * mm});
            skLineSegment(sketch, "E60.right", {"start": v(-13.25, 22.75) * mm, "end": v(-13.25, -82.25) * mm});
            skPoint(sketch, "E60.middle", {"position": v(91.75, -29.75) * mm});
            skPoint(sketch, "E61.visualSharp", {"position": v(-13.25, 30.25) * mm});
            skArc(sketch, "E61.filletArc", {"start": v(-12.25, 30.25) * mm, "mid": v(-12.96, 29.96) * mm, "end": v(-13.25, 29.25) * mm});
            skArc(sketch, "E62.filletArc", {"start": v(-5.75, 30.25) * mm, "mid": v(-11.05, 28.05) * mm, "end": v(-13.25, 22.75) * mm});
            skPoint(sketch, "E63.visualSharp", {"position": v(196.75, 30.25) * mm});
            skArc(sketch, "E63.filletArc", {"start": v(196.75, 22.75) * mm, "mid": v(194.55, 28.05) * mm, "end": v(189.25, 30.25) * mm});
            skPoint(sketch, "E64.visualSharp", {"position": v(196.75, -89.75) * mm});
            skArc(sketch, "E64.filletArc", {"start": v(189.25, -89.75) * mm, "mid": v(194.55, -87.55) * mm, "end": v(196.75, -82.25) * mm});
            skPoint(sketch, "E65.visualSharp", {"position": v(-13.25, -89.75) * mm});
            skArc(sketch, "E65.filletArc", {"start": v(-13.25, -82.25) * mm, "mid": v(-11.05, -87.55) * mm, "end": v(-5.75, -89.75) * mm});
            skSolve(sketch);
        }
        {
            var Q0;
            Q0 = qSketchRegion(id + "F0", true);
            extrude(context, id + "F1", {"entities" : qUnion([Q0]), "depth" : 5 * mm});
        }
        {
            var Q0;
            Q0=makeQuery(id+"F1.opExtrude","CAP_FACE",FACE,{"disambiguationData":[OSD([sQuery(id+"F0.wireOp",EDGE,"E0.bottom"),sQuery(id+"F0.wireOp",EDGE,"E0.top"),sQuery(id+"F0.wireOp",EDGE,"E0.left"),sQuery(id+"F0.wireOp",EDGE,"E0.right"),sQuery(id+"F0.wireOp",EDGE,"E1.filletArc"),sQuery(id+"F0.wireOp",EDGE,"E2.filletArc"),sQuery(id+"F0.wireOp",EDGE,"E3.filletArc"),sQuery(id+"F0.wireOp",EDGE,"E4.filletArc"),sQuery(id+"F0.wireOp",EDGE,"E5.1.0.1"),sQuery(id+"F0.wireOp",EDGE,"E5.1.0.2"),sQuery(id+"F0.wireOp",EDGE,"E5.1.0.3"),sQuery(id+"F0.wireOp",EDGE,"E5.1.0.4"),sQuery(id+"F0.wireOp",EDGE,"E5.1.0.8"),sQuery(id+"F0.wireOp",EDGE,"E5.1.0.9"),sQuery(id+"F0.wireOp",EDGE,"E5.1.0.10"),sQuery(id+"F0.wireOp",EDGE,"E5.1.0.11"),sQuery(id+"F0.wireOp",EDGE,"E5.2.0.1"),sQuery(id+"F0.wireOp",EDGE,"E5.2.0.2"),sQuery(id+"F0.wireOp",EDGE,"E5.2.0.3"),sQuery(id+"F0.wireOp",EDGE,"E5.2.0.4"),sQuery(id+"F0.wireOp",EDGE,"E5.2.0.8"),sQuery(id+"F0.wireOp",EDGE,"E5.2.0.9"),sQuery(id+"F0.wireOp",EDGE,"E5.2.0.10"),sQuery(id+"F0.wireOp",EDGE,"E5.2.0.11"),sQuery(id+"F0.wireOp",EDGE,"E5.3.0.1"),sQuery(id+"F0.wireOp",EDGE,"E5.3.0.2"),sQuery(id+"F0.wireOp",EDGE,"E5.3.0.3"),sQuery(id+"F0.wireOp",EDGE,"E5.3.0.4"),sQuery(id+"F0.wireOp",EDGE,"E5.3.0.8"),sQuery(id+"F0.wireOp",EDGE,"E5.3.0.9"),sQuery(id+"F0.wireOp",EDGE,"E5.3.0.10"),sQuery(id+"F0.wireOp",EDGE,"E5.3.0.11"),sQuery(id+"F0.wireOp",EDGE,"E5.4.0.1"),sQuery(id+"F0.wireOp",EDGE,"E5.4.0.2"),sQuery(id+"F0.wireOp",EDGE,"E5.4.0.3"),sQuery(id+"F0.wireOp",EDGE,"E5.4.0.4"),sQuery(id+"F0.wireOp",EDGE,"E5.4.0.8"),sQuery(id+"F0.wireOp",EDGE,"E5.4.0.9"),sQuery(id+"F0.wireOp",EDGE,"E5.4.0.10"),sQuery(id+"F0.wireOp",EDGE,"E5.4.0.11"),sQuery(id+"F0.wireOp",EDGE,"E5.5.0.1"),sQuery(id+"F0.wireOp",EDGE,"E5.5.0.2"),sQuery(id+"F0.wireOp",EDGE,"E5.5.0.3"),sQuery(id+"F0.wireOp",EDGE,"E5.5.0.4"),sQuery(id+"F0.wireOp",EDGE,"E5.5.0.8"),sQuery(id+"F0.wireOp",EDGE,"E5.5.0.9"),sQuery(id+"F0.wireOp",EDGE,"E5.5.0.10"),sQuery(id+"F0.wireOp",EDGE,"E5.5.0.11"),sQuery(id+"F0.wireOp",EDGE,"E5.6.0.1"),sQuery(id+"F0.wireOp",EDGE,"E5.6.0.2"),sQuery(id+"F0.wireOp",EDGE,"E5.6.0.3"),sQuery(id+"F0.wireOp",EDGE,"E5.6.0.4"),sQuery(id+"F0.wireOp",EDGE,"E5.6.0.8"),sQuery(id+"F0.wireOp",EDGE,"E5.6.0.9"),sQuery(id+"F0.wireOp",EDGE,"E5.6.0.10"),sQuery(id+"F0.wireOp",EDGE,"E5.6.0.11"),sQuery(id+"F0.wireOp",EDGE,"E5.7.0.1"),sQuery(id+"F0.wireOp",EDGE,"E5.7.0.2"),sQuery(id+"F0.wireOp",EDGE,"E5.7.0.3"),sQuery(id+"F0.wireOp",EDGE,"E5.7.0.4"),sQuery(id+"F0.wireOp",EDGE,"E5.7.0.8"),sQuery(id+"F0.wireOp",EDGE,"E5.7.0.9"),sQuery(id+"F0.wireOp",EDGE,"E5.7.0.10"),sQuery(id+"F0.wireOp",EDGE,"E5.7.0.11"),sQuery(id+"F0.wireOp",EDGE,"E5.8.0.1"),sQuery(id+"F0.wireOp",EDGE,"E5.8.0.2"),sQuery(id+"F0.wireOp",EDGE,"E5.8.0.3"),sQuery(id+"F0.wireOp",EDGE,"E5.8.0.4"),sQuery(id+"F0.wireOp",EDGE,"E5.8.0.8"),sQuery(id+"F0.wireOp",EDGE,"E5.8.0.9"),sQuery(id+"F0.wireOp",EDGE,"E5.8.0.10"),sQuery(id+"F0.wireOp",EDGE,"E5.8.0.11"),sQuery(id+"F0.wireOp",EDGE,"E5.9.0.1"),sQuery(id+"F0.wireOp",EDGE,"E5.9.0.2"),sQuery(id+"F0.wireOp",EDGE,"E5.9.0.3"),sQuery(id+"F0.wireOp",EDGE,"E5.9.0.4"),sQuery(id+"F0.wireOp",EDGE,"E5.9.0.8"),sQuery(id+"F0.wireOp",EDGE,"E5.9.0.9"),sQuery(id+"F0.wireOp",EDGE,"E5.9.0.10"),sQuery(id+"F0.wireOp",EDGE,"E5.9.0.11"),sQuery(id+"F0.wireOp",EDGE,"E5.10.0.1"),sQuery(id+"F0.wireOp",EDGE,"E5.10.0.2"),sQuery(id+"F0.wireOp",EDGE,"E5.10.0.3"),sQuery(id+"F0.wireOp",EDGE,"E5.10.0.4"),sQuery(id+"F0.wireOp",EDGE,"E5.10.0.8"),sQuery(id+"F0.wireOp",EDGE,"E5.10.0.9"),sQuery(id+"F0.wireOp",EDGE,"E5.10.0.10"),sQuery(id+"F0.wireOp",EDGE,"E5.10.0.11"),sQuery(id+"F0.wireOp",EDGE,"E5.11.0.1"),sQuery(id+"F0.wireOp",EDGE,"E5.11.0.2"),sQuery(id+"F0.wireOp",EDGE,"E5.11.0.3"),sQuery(id+"F0.wireOp",EDGE,"E5.11.0.4"),sQuery(id+"F0.wireOp",EDGE,"E5.11.0.8"),sQuery(id+"F0.wireOp",EDGE,"E5.11.0.9"),sQuery(id+"F0.wireOp",EDGE,"E5.11.0.10"),sQuery(id+"F0.wireOp",EDGE,"E5.11.0.11"),sQuery(id+"F0.wireOp",EDGE,"E6.0.1.0"),sQuery(id+"F0.wireOp",EDGE,"E6.0.1.3"),sQuery(id+"F0.wireOp",EDGE,"E6.0.1.5"),sQuery(id+"F0.wireOp",EDGE,"E6.0.1.6"),sQuery(id+"F0.wireOp",EDGE,"E6.0.1.7"),sQuery(id+"F0.wireOp",EDGE,"E6.0.1.9"),sQuery(id+"F0.wireOp",EDGE,"E6.0.1.10"),sQuery(id+"F0.wireOp",EDGE,"E6.0.1.11"),sQuery(id+"F0.wireOp",EDGE,"E6.0.1.13"),sQuery(id+"F0.wireOp",EDGE,"E6.0.1.14"),sQuery(id+"F0.wireOp",EDGE,"E6.0.1.17"),sQuery(id+"F0.wireOp",EDGE,"E6.0.1.19"),sQuery(id+"F0.wireOp",EDGE,"E6.0.1.20"),sQuery(id+"F0.wireOp",EDGE,"E6.0.1.22"),sQuery(id+"F0.wireOp",EDGE,"E6.0.1.24"),sQuery(id+"F0.wireOp",EDGE,"E6.0.1.25"),sQuery(id+"F0.wireOp",EDGE,"E6.0.1.28"),sQuery(id+"F0.wireOp",EDGE,"E6.0.1.29"),sQuery(id+"F0.wireOp",EDGE,"E6.0.1.30"),sQuery(id+"F0.wireOp",EDGE,"E6.0.1.33"),sQuery(id+"F0.wireOp",EDGE,"E6.0.1.34"),sQuery(id+"F0.wireOp",EDGE,"E6.0.1.35"),sQuery(id+"F0.wireOp",EDGE,"E6.0.1.36"),sQuery(id+"F0.wireOp",EDGE,"E6.0.1.39"),sQuery(id+"F0.wireOp",EDGE,"E6.0.1.40"),sQuery(id+"F0.wireOp",EDGE,"E6.0.1.41"),sQuery(id+"F0.wireOp",EDGE,"E6.0.1.42"),sQuery(id+"F0.wireOp",EDGE,"E6.0.1.43"),sQuery(id+"F0.wireOp",EDGE,"E6.0.1.44"),sQuery(id+"F0.wireOp",EDGE,"E6.0.1.46"),sQuery(id+"F0.wireOp",EDGE,"E6.0.1.55"),sQuery(id+"F0.wireOp",EDGE,"E6.0.1.57"),sQuery(id+"F0.wireOp",EDGE,"E6.0.1.58"),sQuery(id+"F0.wireOp",EDGE,"E6.0.1.59"),sQuery(id+"F0.wireOp",EDGE,"E6.0.1.60"),sQuery(id+"F0.wireOp",EDGE,"E6.0.1.61"),sQuery(id+"F0.wireOp",EDGE,"E6.0.1.62"),sQuery(id+"F0.wireOp",EDGE,"E6.0.1.65"),sQuery(id+"F0.wireOp",EDGE,"E6.0.1.66"),sQuery(id+"F0.wireOp",EDGE,"E6.0.1.67"),sQuery(id+"F0.wireOp",EDGE,"E6.0.1.68"),sQuery(id+"F0.wireOp",EDGE,"E6.0.1.69"),sQuery(id+"F0.wireOp",EDGE,"E6.0.1.71"),sQuery(id+"F0.wireOp",EDGE,"E6.0.1.72"),sQuery(id+"F0.wireOp",EDGE,"E6.0.1.73"),sQuery(id+"F0.wireOp",EDGE,"E6.0.1.74"),sQuery(id+"F0.wireOp",EDGE,"E6.0.1.75"),sQuery(id+"F0.wireOp",EDGE,"E6.0.1.76"),sQuery(id+"F0.wireOp",EDGE,"E6.0.1.77"),sQuery(id+"F0.wireOp",EDGE,"E6.0.1.78"),sQuery(id+"F0.wireOp",EDGE,"E6.0.1.79"),sQuery(id+"F0.wireOp",EDGE,"E6.0.1.80"),sQuery(id+"F0.wireOp",EDGE,"E6.0.1.81"),sQuery(id+"F0.wireOp",EDGE,"E6.0.1.82"),sQuery(id+"F0.wireOp",EDGE,"E6.0.1.83"),sQuery(id+"F0.wireOp",EDGE,"E6.0.1.84"),sQuery(id+"F0.wireOp",EDGE,"E6.0.1.85"),sQuery(id+"F0.wireOp",EDGE,"E6.0.1.86"),sQuery(id+"F0.wireOp",EDGE,"E6.0.1.87"),sQuery(id+"F0.wireOp",EDGE,"E6.0.1.88"),sQuery(id+"F0.wireOp",EDGE,"E6.0.1.89"),sQuery(id+"F0.wireOp",EDGE,"E6.0.1.90"),sQuery(id+"F0.wireOp",EDGE,"E6.0.1.92"),sQuery(id+"F0.wireOp",EDGE,"E6.0.1.93"),sQuery(id+"F0.wireOp",EDGE,"E6.0.1.94"),sQuery(id+"F0.wireOp",EDGE,"E6.0.1.95"),sQuery(id+"F0.wireOp",EDGE,"E6.0.1.97"),sQuery(id+"F0.wireOp",EDGE,"E6.0.1.98"),sQuery(id+"F0.wireOp",EDGE,"E6.0.1.99"),sQuery(id+"F0.wireOp",EDGE,"E6.0.1.100"),sQuery(id+"F0.wireOp",EDGE,"E6.0.1.101"),sQuery(id+"F0.wireOp",EDGE,"E6.0.1.102"),sQuery(id+"F0.wireOp",EDGE,"E6.0.1.103"),sQuery(id+"F0.wireOp",EDGE,"E6.0.1.104"),sQuery(id+"F0.wireOp",EDGE,"E6.0.1.105"),sQuery(id+"F0.wireOp",EDGE,"E6.0.1.106"),sQuery(id+"F0.wireOp",EDGE,"E6.0.1.107"),sQuery(id+"F0.wireOp",EDGE,"E6.0.1.108"),sQuery(id+"F0.wireOp",EDGE,"E6.0.1.110"),sQuery(id+"F0.wireOp",EDGE,"E6.0.1.111"),sQuery(id+"F0.wireOp",EDGE,"E6.0.1.112"),sQuery(id+"F0.wireOp",EDGE,"E6.0.1.113"),sQuery(id+"F0.wireOp",EDGE,"E6.0.1.114"),sQuery(id+"F0.wireOp",EDGE,"E6.0.1.115"),sQuery(id+"F0.wireOp",EDGE,"E6.0.1.117"),sQuery(id+"F0.wireOp",EDGE,"E6.0.1.118"),sQuery(id+"F0.wireOp",EDGE,"E6.0.1.119"),sQuery(id+"F0.wireOp",EDGE,"E6.0.1.120"),sQuery(id+"F0.wireOp",EDGE,"E6.0.2.0"),sQuery(id+"F0.wireOp",EDGE,"E6.0.2.3"),sQuery(id+"F0.wireOp",EDGE,"E6.0.2.4"),sQuery(id+"F0.wireOp",EDGE,"E6.0.2.5"),sQuery(id+"F0.wireOp",EDGE,"E6.0.2.6"),sQuery(id+"F0.wireOp",EDGE,"E6.0.2.7"),sQuery(id+"F0.wireOp",EDGE,"E6.0.2.9"),sQuery(id+"F0.wireOp",EDGE,"E6.0.2.10"),sQuery(id+"F0.wireOp",EDGE,"E6.0.2.11"),sQuery(id+"F0.wireOp",EDGE,"E6.0.2.12"),sQuery(id+"F0.wireOp",EDGE,"E6.0.2.13"),sQuery(id+"F0.wireOp",EDGE,"E6.0.2.14"),sQuery(id+"F0.wireOp",EDGE,"E6.0.2.17"),sQuery(id+"F0.wireOp",EDGE,"E6.0.2.18"),sQuery(id+"F0.wireOp",EDGE,"E6.0.2.19"),sQuery(id+"F0.wireOp",EDGE,"E6.0.2.20"),sQuery(id+"F0.wireOp",EDGE,"E6.0.2.22"),sQuery(id+"F0.wireOp",EDGE,"E6.0.2.24"),sQuery(id+"F0.wireOp",EDGE,"E6.0.2.25"),sQuery(id+"F0.wireOp",EDGE,"E6.0.2.28"),sQuery(id+"F0.wireOp",EDGE,"E6.0.2.29"),sQuery(id+"F0.wireOp",EDGE,"E6.0.2.30"),sQuery(id+"F0.wireOp",EDGE,"E6.0.2.33"),sQuery(id+"F0.wireOp",EDGE,"E6.0.2.34"),sQuery(id+"F0.wireOp",EDGE,"E6.0.2.35"),sQuery(id+"F0.wireOp",EDGE,"E6.0.2.36"),sQuery(id+"F0.wireOp",EDGE,"E6.0.2.39"),sQuery(id+"F0.wireOp",EDGE,"E6.0.2.41"),sQuery(id+"F0.wireOp",EDGE,"E6.0.2.42"),sQuery(id+"F0.wireOp",EDGE,"E6.0.2.44"),sQuery(id+"F0.wireOp",EDGE,"E6.0.2.46"),sQuery(id+"F0.wireOp",EDGE,"E6.0.2.55"),sQuery(id+"F0.wireOp",EDGE,"E6.0.2.57"),sQuery(id+"F0.wireOp",EDGE,"E6.0.2.58"),sQuery(id+"F0.wireOp",EDGE,"E6.0.2.59"),sQuery(id+"F0.wireOp",EDGE,"E6.0.2.60"),sQuery(id+"F0.wireOp",EDGE,"E6.0.2.61"),sQuery(id+"F0.wireOp",EDGE,"E6.0.2.62"),sQuery(id+"F0.wireOp",EDGE,"E6.0.2.63"),sQuery(id+"F0.wireOp",EDGE,"E6.0.2.65"),sQuery(id+"F0.wireOp",EDGE,"E6.0.2.66"),sQuery(id+"F0.wireOp",EDGE,"E6.0.2.67"),sQuery(id+"F0.wireOp",EDGE,"E6.0.2.68"),sQuery(id+"F0.wireOp",EDGE,"E6.0.2.69"),sQuery(id+"F0.wireOp",EDGE,"E6.0.2.71"),sQuery(id+"F0.wireOp",EDGE,"E6.0.2.72"),sQuery(id+"F0.wireOp",EDGE,"E6.0.2.73"),sQuery(id+"F0.wireOp",EDGE,"E6.0.2.74"),sQuery(id+"F0.wireOp",EDGE,"E6.0.2.75"),sQuery(id+"F0.wireOp",EDGE,"E6.0.2.76"),sQuery(id+"F0.wireOp",EDGE,"E6.0.2.77"),sQuery(id+"F0.wireOp",EDGE,"E6.0.2.78"),sQuery(id+"F0.wireOp",EDGE,"E6.0.2.79"),sQuery(id+"F0.wireOp",EDGE,"E6.0.2.80"),sQuery(id+"F0.wireOp",EDGE,"E6.0.2.81"),sQuery(id+"F0.wireOp",EDGE,"E6.0.2.82"),sQuery(id+"F0.wireOp",EDGE,"E6.0.2.83"),sQuery(id+"F0.wireOp",EDGE,"E6.0.2.84"),sQuery(id+"F0.wireOp",EDGE,"E6.0.2.85"),sQuery(id+"F0.wireOp",EDGE,"E6.0.2.86"),sQuery(id+"F0.wireOp",EDGE,"E6.0.2.89"),sQuery(id+"F0.wireOp",EDGE,"E6.0.2.90"),sQuery(id+"F0.wireOp",EDGE,"E6.0.2.91"),sQuery(id+"F0.wireOp",EDGE,"E6.0.2.92"),sQuery(id+"F0.wireOp",EDGE,"E6.0.2.93"),sQuery(id+"F0.wireOp",EDGE,"E6.0.2.94"),sQuery(id+"F0.wireOp",EDGE,"E6.0.2.96"),sQuery(id+"F0.wireOp",EDGE,"E6.0.2.97"),sQuery(id+"F0.wireOp",EDGE,"E6.0.2.98"),sQuery(id+"F0.wireOp",EDGE,"E6.0.2.99"),sQuery(id+"F0.wireOp",EDGE,"E6.0.2.100"),sQuery(id+"F0.wireOp",EDGE,"E6.0.2.101"),sQuery(id+"F0.wireOp",EDGE,"E6.0.2.102"),sQuery(id+"F0.wireOp",EDGE,"E6.0.2.103"),sQuery(id+"F0.wireOp",EDGE,"E6.0.2.104"),sQuery(id+"F0.wireOp",EDGE,"E6.0.2.105"),sQuery(id+"F0.wireOp",EDGE,"E6.0.2.106"),sQuery(id+"F0.wireOp",EDGE,"E6.0.2.107"),sQuery(id+"F0.wireOp",EDGE,"E6.0.2.108"),sQuery(id+"F0.wireOp",EDGE,"E6.0.2.109"),sQuery(id+"F0.wireOp",EDGE,"E6.0.2.110"),sQuery(id+"F0.wireOp",EDGE,"E6.0.2.113"),sQuery(id+"F0.wireOp",EDGE,"E6.0.2.114"),sQuery(id+"F0.wireOp",EDGE,"E6.0.2.115"),sQuery(id+"F0.wireOp",EDGE,"E6.0.2.116"),sQuery(id+"F0.wireOp",EDGE,"E6.0.2.117"),sQuery(id+"F0.wireOp",EDGE,"E6.0.2.118"),sQuery(id+"F0.wireOp",EDGE,"E6.0.2.119"),sQuery(id+"F0.wireOp",EDGE,"E6.0.2.120"),sQuery(id+"F0.wireOp",EDGE,"E7"),sQuery(id+"F0.wireOp",EDGE,"E8"),sQuery(id+"F0.wireOp",EDGE,"E9"),sQuery(id+"F0.wireOp",EDGE,"E13.bottom"),sQuery(id+"F0.wireOp",EDGE,"E13.top"),sQuery(id+"F0.wireOp",EDGE,"E13.left"),sQuery(id+"F0.wireOp",EDGE,"E13.right"),sQuery(id+"F0.wireOp",EDGE,"E14.filletArc"),sQuery(id+"F0.wireOp",EDGE,"E15.filletArc"),sQuery(id+"F0.wireOp",EDGE,"E16.filletArc"),sQuery(id+"F0.wireOp",EDGE,"E17.filletArc"),sQuery(id+"F0.wireOp",EDGE,"E19.bottom"),sQuery(id+"F0.wireOp",EDGE,"E19.top"),sQuery(id+"F0.wireOp",EDGE,"E19.left"),sQuery(id+"F0.wireOp",EDGE,"E19.right"),sQuery(id+"F0.wireOp",EDGE,"E20"),sQuery(id+"F0.wireOp",EDGE,"E21.filletArc"),sQuery(id+"F0.wireOp",EDGE,"E22.filletArc"),sQuery(id+"F0.wireOp",EDGE,"E23.filletArc"),sQuery(id+"F0.wireOp",EDGE,"E24.filletArc"),sQuery(id+"F0.wireOp",EDGE,"E26.bottom"),sQuery(id+"F0.wireOp",EDGE,"E26.top"),sQuery(id+"F0.wireOp",EDGE,"E26.left"),sQuery(id+"F0.wireOp",EDGE,"E26.right"),sQuery(id+"F0.wireOp",EDGE,"E27.filletArc"),sQuery(id+"F0.wireOp",EDGE,"E28.filletArc"),sQuery(id+"F0.wireOp",EDGE,"E29.filletArc"),sQuery(id+"F0.wireOp",EDGE,"E30.filletArc"),sQuery(id+"F0.wireOp",EDGE,"E31.MirrorCS"),sQuery(id+"F0.wireOp",EDGE,"E32.MirrorCS"),sQuery(id+"F0.wireOp",EDGE,"E33.MirrorCS"),sQuery(id+"F0.wireOp",EDGE,"E34.MirrorCS"),sQuery(id+"F0.wireOp",EDGE,"E35.MirrorCS"),sQuery(id+"F0.wireOp",EDGE,"E36.MirrorCS"),sQuery(id+"F0.wireOp",EDGE,"E37.MirrorCS"),sQuery(id+"F0.wireOp",EDGE,"E38.MirrorCS"),sQuery(id+"F0.wireOp",EDGE,"E39.MirrorCS"),sQuery(id+"F0.wireOp",EDGE,"E44.MirrorCS"),sQuery(id+"F0.wireOp",EDGE,"E46.MirrorCS"),sQuery(id+"F0.wireOp",EDGE,"E47.MirrorCS"),sQuery(id+"F0.wireOp",EDGE,"E48.MirrorCS"),sQuery(id+"F0.wireOp",EDGE,"E49.MirrorCS"),sQuery(id+"F0.wireOp",EDGE,"E53.MirrorCS"),sQuery(id+"F0.wireOp",EDGE,"E54.MirrorCS"),sQuery(id+"F0.wireOp",EDGE,"E57.MirrorCS"),sQuery(id+"F0.wireOp",EDGE,"E60.bottom"),sQuery(id+"F0.wireOp",EDGE,"E60.top"),sQuery(id+"F0.wireOp",EDGE,"E60.left"),sQuery(id+"F0.wireOp",EDGE,"E60.right"),sQuery(id+"F0.wireOp",EDGE,"E62.filletArc"),sQuery(id+"F0.wireOp",EDGE,"E63.filletArc"),sQuery(id+"F0.wireOp",EDGE,"E64.filletArc"),sQuery(id+"F0.wireOp",EDGE,"E65.filletArc")])],"isStart":false});
            var sketch = newSketch(context, id + "F2", { "sketchPlane" : qUnion([Q0])});
            skLineSegment(sketch, "E66", {"start": v(-13.25, -82.25) * mm, "end": v(-13.25, -90.05) * mm});
            skLineSegment(sketch, "E67", {"start": v(-13.25, -82.25) * mm, "end": v(196.75, -82.25) * mm});
            skLineSegment(sketch, "E68", {"start": v(196.75, -82.25) * mm, "end": v(196.75, -90.05) * mm});
            skLineSegment(sketch, "E69", {"start": v(189.25, -97.55) * mm, "end": v(-5.75, -97.55) * mm});
            skPoint(sketch, "E70.visualSharp", {"position": v(-13.25, -97.55) * mm});
            skArc(sketch, "E70.filletArc", {"start": v(-13.25, -90.05) * mm, "mid": v(-11.05, -95.35) * mm, "end": v(-5.75, -97.55) * mm});
            skPoint(sketch, "E71.visualSharp", {"position": v(196.75, -97.55) * mm});
            skArc(sketch, "E71.filletArc", {"start": v(189.25, -97.55) * mm, "mid": v(194.55, -95.35) * mm, "end": v(196.75, -90.05) * mm});
            skSolve(sketch);
        }
        {
            var Q0;
            Q0 = qSketchRegion(id + "F2", true);
            var Q1;
            Q1=makeQuery(id+"F1.opExtrude","CAP_FACE",FACE,{"disambiguationData":[OSD([sQuery(id+"F0.wireOp",EDGE,"E0.bottom"),sQuery(id+"F0.wireOp",EDGE,"E0.top"),sQuery(id+"F0.wireOp",EDGE,"E0.left"),sQuery(id+"F0.wireOp",EDGE,"E0.right"),sQuery(id+"F0.wireOp",EDGE,"E1.filletArc"),sQuery(id+"F0.wireOp",EDGE,"E2.filletArc"),sQuery(id+"F0.wireOp",EDGE,"E3.filletArc"),sQuery(id+"F0.wireOp",EDGE,"E4.filletArc"),sQuery(id+"F0.wireOp",EDGE,"E5.1.0.1"),sQuery(id+"F0.wireOp",EDGE,"E5.1.0.2"),sQuery(id+"F0.wireOp",EDGE,"E5.1.0.3"),sQuery(id+"F0.wireOp",EDGE,"E5.1.0.4"),sQuery(id+"F0.wireOp",EDGE,"E5.1.0.8"),sQuery(id+"F0.wireOp",EDGE,"E5.1.0.9"),sQuery(id+"F0.wireOp",EDGE,"E5.1.0.10"),sQuery(id+"F0.wireOp",EDGE,"E5.1.0.11"),sQuery(id+"F0.wireOp",EDGE,"E5.2.0.1"),sQuery(id+"F0.wireOp",EDGE,"E5.2.0.2"),sQuery(id+"F0.wireOp",EDGE,"E5.2.0.3"),sQuery(id+"F0.wireOp",EDGE,"E5.2.0.4"),sQuery(id+"F0.wireOp",EDGE,"E5.2.0.8"),sQuery(id+"F0.wireOp",EDGE,"E5.2.0.9"),sQuery(id+"F0.wireOp",EDGE,"E5.2.0.10"),sQuery(id+"F0.wireOp",EDGE,"E5.2.0.11"),sQuery(id+"F0.wireOp",EDGE,"E5.3.0.1"),sQuery(id+"F0.wireOp",EDGE,"E5.3.0.2"),sQuery(id+"F0.wireOp",EDGE,"E5.3.0.3"),sQuery(id+"F0.wireOp",EDGE,"E5.3.0.4"),sQuery(id+"F0.wireOp",EDGE,"E5.3.0.8"),sQuery(id+"F0.wireOp",EDGE,"E5.3.0.9"),sQuery(id+"F0.wireOp",EDGE,"E5.3.0.10"),sQuery(id+"F0.wireOp",EDGE,"E5.3.0.11"),sQuery(id+"F0.wireOp",EDGE,"E5.4.0.1"),sQuery(id+"F0.wireOp",EDGE,"E5.4.0.2"),sQuery(id+"F0.wireOp",EDGE,"E5.4.0.3"),sQuery(id+"F0.wireOp",EDGE,"E5.4.0.4"),sQuery(id+"F0.wireOp",EDGE,"E5.4.0.8"),sQuery(id+"F0.wireOp",EDGE,"E5.4.0.9"),sQuery(id+"F0.wireOp",EDGE,"E5.4.0.10"),sQuery(id+"F0.wireOp",EDGE,"E5.4.0.11"),sQuery(id+"F0.wireOp",EDGE,"E5.5.0.1"),sQuery(id+"F0.wireOp",EDGE,"E5.5.0.2"),sQuery(id+"F0.wireOp",EDGE,"E5.5.0.3"),sQuery(id+"F0.wireOp",EDGE,"E5.5.0.4"),sQuery(id+"F0.wireOp",EDGE,"E5.5.0.8"),sQuery(id+"F0.wireOp",EDGE,"E5.5.0.9"),sQuery(id+"F0.wireOp",EDGE,"E5.5.0.10"),sQuery(id+"F0.wireOp",EDGE,"E5.5.0.11"),sQuery(id+"F0.wireOp",EDGE,"E5.6.0.1"),sQuery(id+"F0.wireOp",EDGE,"E5.6.0.2"),sQuery(id+"F0.wireOp",EDGE,"E5.6.0.3"),sQuery(id+"F0.wireOp",EDGE,"E5.6.0.4"),sQuery(id+"F0.wireOp",EDGE,"E5.6.0.8"),sQuery(id+"F0.wireOp",EDGE,"E5.6.0.9"),sQuery(id+"F0.wireOp",EDGE,"E5.6.0.10"),sQuery(id+"F0.wireOp",EDGE,"E5.6.0.11"),sQuery(id+"F0.wireOp",EDGE,"E5.7.0.1"),sQuery(id+"F0.wireOp",EDGE,"E5.7.0.2"),sQuery(id+"F0.wireOp",EDGE,"E5.7.0.3"),sQuery(id+"F0.wireOp",EDGE,"E5.7.0.4"),sQuery(id+"F0.wireOp",EDGE,"E5.7.0.8"),sQuery(id+"F0.wireOp",EDGE,"E5.7.0.9"),sQuery(id+"F0.wireOp",EDGE,"E5.7.0.10"),sQuery(id+"F0.wireOp",EDGE,"E5.7.0.11"),sQuery(id+"F0.wireOp",EDGE,"E5.8.0.1"),sQuery(id+"F0.wireOp",EDGE,"E5.8.0.2"),sQuery(id+"F0.wireOp",EDGE,"E5.8.0.3"),sQuery(id+"F0.wireOp",EDGE,"E5.8.0.4"),sQuery(id+"F0.wireOp",EDGE,"E5.8.0.8"),sQuery(id+"F0.wireOp",EDGE,"E5.8.0.9"),sQuery(id+"F0.wireOp",EDGE,"E5.8.0.10"),sQuery(id+"F0.wireOp",EDGE,"E5.8.0.11"),sQuery(id+"F0.wireOp",EDGE,"E5.9.0.1"),sQuery(id+"F0.wireOp",EDGE,"E5.9.0.2"),sQuery(id+"F0.wireOp",EDGE,"E5.9.0.3"),sQuery(id+"F0.wireOp",EDGE,"E5.9.0.4"),sQuery(id+"F0.wireOp",EDGE,"E5.9.0.8"),sQuery(id+"F0.wireOp",EDGE,"E5.9.0.9"),sQuery(id+"F0.wireOp",EDGE,"E5.9.0.10"),sQuery(id+"F0.wireOp",EDGE,"E5.9.0.11"),sQuery(id+"F0.wireOp",EDGE,"E5.10.0.1"),sQuery(id+"F0.wireOp",EDGE,"E5.10.0.2"),sQuery(id+"F0.wireOp",EDGE,"E5.10.0.3"),sQuery(id+"F0.wireOp",EDGE,"E5.10.0.4"),sQuery(id+"F0.wireOp",EDGE,"E5.10.0.8"),sQuery(id+"F0.wireOp",EDGE,"E5.10.0.9"),sQuery(id+"F0.wireOp",EDGE,"E5.10.0.10"),sQuery(id+"F0.wireOp",EDGE,"E5.10.0.11"),sQuery(id+"F0.wireOp",EDGE,"E5.11.0.1"),sQuery(id+"F0.wireOp",EDGE,"E5.11.0.2"),sQuery(id+"F0.wireOp",EDGE,"E5.11.0.3"),sQuery(id+"F0.wireOp",EDGE,"E5.11.0.4"),sQuery(id+"F0.wireOp",EDGE,"E5.11.0.8"),sQuery(id+"F0.wireOp",EDGE,"E5.11.0.9"),sQuery(id+"F0.wireOp",EDGE,"E5.11.0.10"),sQuery(id+"F0.wireOp",EDGE,"E5.11.0.11"),sQuery(id+"F0.wireOp",EDGE,"E6.0.1.0"),sQuery(id+"F0.wireOp",EDGE,"E6.0.1.3"),sQuery(id+"F0.wireOp",EDGE,"E6.0.1.5"),sQuery(id+"F0.wireOp",EDGE,"E6.0.1.6"),sQuery(id+"F0.wireOp",EDGE,"E6.0.1.7"),sQuery(id+"F0.wireOp",EDGE,"E6.0.1.9"),sQuery(id+"F0.wireOp",EDGE,"E6.0.1.10"),sQuery(id+"F0.wireOp",EDGE,"E6.0.1.11"),sQuery(id+"F0.wireOp",EDGE,"E6.0.1.13"),sQuery(id+"F0.wireOp",EDGE,"E6.0.1.14"),sQuery(id+"F0.wireOp",EDGE,"E6.0.1.17"),sQuery(id+"F0.wireOp",EDGE,"E6.0.1.19"),sQuery(id+"F0.wireOp",EDGE,"E6.0.1.20"),sQuery(id+"F0.wireOp",EDGE,"E6.0.1.22"),sQuery(id+"F0.wireOp",EDGE,"E6.0.1.24"),sQuery(id+"F0.wireOp",EDGE,"E6.0.1.25"),sQuery(id+"F0.wireOp",EDGE,"E6.0.1.28"),sQuery(id+"F0.wireOp",EDGE,"E6.0.1.29"),sQuery(id+"F0.wireOp",EDGE,"E6.0.1.30"),sQuery(id+"F0.wireOp",EDGE,"E6.0.1.33"),sQuery(id+"F0.wireOp",EDGE,"E6.0.1.34"),sQuery(id+"F0.wireOp",EDGE,"E6.0.1.35"),sQuery(id+"F0.wireOp",EDGE,"E6.0.1.36"),sQuery(id+"F0.wireOp",EDGE,"E6.0.1.39"),sQuery(id+"F0.wireOp",EDGE,"E6.0.1.40"),sQuery(id+"F0.wireOp",EDGE,"E6.0.1.41"),sQuery(id+"F0.wireOp",EDGE,"E6.0.1.42"),sQuery(id+"F0.wireOp",EDGE,"E6.0.1.43"),sQuery(id+"F0.wireOp",EDGE,"E6.0.1.44"),sQuery(id+"F0.wireOp",EDGE,"E6.0.1.46"),sQuery(id+"F0.wireOp",EDGE,"E6.0.1.55"),sQuery(id+"F0.wireOp",EDGE,"E6.0.1.57"),sQuery(id+"F0.wireOp",EDGE,"E6.0.1.58"),sQuery(id+"F0.wireOp",EDGE,"E6.0.1.59"),sQuery(id+"F0.wireOp",EDGE,"E6.0.1.60"),sQuery(id+"F0.wireOp",EDGE,"E6.0.1.61"),sQuery(id+"F0.wireOp",EDGE,"E6.0.1.62"),sQuery(id+"F0.wireOp",EDGE,"E6.0.1.65"),sQuery(id+"F0.wireOp",EDGE,"E6.0.1.66"),sQuery(id+"F0.wireOp",EDGE,"E6.0.1.67"),sQuery(id+"F0.wireOp",EDGE,"E6.0.1.68"),sQuery(id+"F0.wireOp",EDGE,"E6.0.1.69"),sQuery(id+"F0.wireOp",EDGE,"E6.0.1.71"),sQuery(id+"F0.wireOp",EDGE,"E6.0.1.72"),sQuery(id+"F0.wireOp",EDGE,"E6.0.1.73"),sQuery(id+"F0.wireOp",EDGE,"E6.0.1.74"),sQuery(id+"F0.wireOp",EDGE,"E6.0.1.75"),sQuery(id+"F0.wireOp",EDGE,"E6.0.1.76"),sQuery(id+"F0.wireOp",EDGE,"E6.0.1.77"),sQuery(id+"F0.wireOp",EDGE,"E6.0.1.78"),sQuery(id+"F0.wireOp",EDGE,"E6.0.1.79"),sQuery(id+"F0.wireOp",EDGE,"E6.0.1.80"),sQuery(id+"F0.wireOp",EDGE,"E6.0.1.81"),sQuery(id+"F0.wireOp",EDGE,"E6.0.1.82"),sQuery(id+"F0.wireOp",EDGE,"E6.0.1.83"),sQuery(id+"F0.wireOp",EDGE,"E6.0.1.84"),sQuery(id+"F0.wireOp",EDGE,"E6.0.1.85"),sQuery(id+"F0.wireOp",EDGE,"E6.0.1.86"),sQuery(id+"F0.wireOp",EDGE,"E6.0.1.87"),sQuery(id+"F0.wireOp",EDGE,"E6.0.1.88"),sQuery(id+"F0.wireOp",EDGE,"E6.0.1.89"),sQuery(id+"F0.wireOp",EDGE,"E6.0.1.90"),sQuery(id+"F0.wireOp",EDGE,"E6.0.1.92"),sQuery(id+"F0.wireOp",EDGE,"E6.0.1.93"),sQuery(id+"F0.wireOp",EDGE,"E6.0.1.94"),sQuery(id+"F0.wireOp",EDGE,"E6.0.1.95"),sQuery(id+"F0.wireOp",EDGE,"E6.0.1.97"),sQuery(id+"F0.wireOp",EDGE,"E6.0.1.98"),sQuery(id+"F0.wireOp",EDGE,"E6.0.1.99"),sQuery(id+"F0.wireOp",EDGE,"E6.0.1.100"),sQuery(id+"F0.wireOp",EDGE,"E6.0.1.101"),sQuery(id+"F0.wireOp",EDGE,"E6.0.1.102"),sQuery(id+"F0.wireOp",EDGE,"E6.0.1.103"),sQuery(id+"F0.wireOp",EDGE,"E6.0.1.104"),sQuery(id+"F0.wireOp",EDGE,"E6.0.1.105"),sQuery(id+"F0.wireOp",EDGE,"E6.0.1.106"),sQuery(id+"F0.wireOp",EDGE,"E6.0.1.107"),sQuery(id+"F0.wireOp",EDGE,"E6.0.1.108"),sQuery(id+"F0.wireOp",EDGE,"E6.0.1.110"),sQuery(id+"F0.wireOp",EDGE,"E6.0.1.111"),sQuery(id+"F0.wireOp",EDGE,"E6.0.1.112"),sQuery(id+"F0.wireOp",EDGE,"E6.0.1.113"),sQuery(id+"F0.wireOp",EDGE,"E6.0.1.114"),sQuery(id+"F0.wireOp",EDGE,"E6.0.1.115"),sQuery(id+"F0.wireOp",EDGE,"E6.0.1.117"),sQuery(id+"F0.wireOp",EDGE,"E6.0.1.118"),sQuery(id+"F0.wireOp",EDGE,"E6.0.1.119"),sQuery(id+"F0.wireOp",EDGE,"E6.0.1.120"),sQuery(id+"F0.wireOp",EDGE,"E6.0.2.0"),sQuery(id+"F0.wireOp",EDGE,"E6.0.2.3"),sQuery(id+"F0.wireOp",EDGE,"E6.0.2.4"),sQuery(id+"F0.wireOp",EDGE,"E6.0.2.5"),sQuery(id+"F0.wireOp",EDGE,"E6.0.2.6"),sQuery(id+"F0.wireOp",EDGE,"E6.0.2.7"),sQuery(id+"F0.wireOp",EDGE,"E6.0.2.9"),sQuery(id+"F0.wireOp",EDGE,"E6.0.2.10"),sQuery(id+"F0.wireOp",EDGE,"E6.0.2.11"),sQuery(id+"F0.wireOp",EDGE,"E6.0.2.12"),sQuery(id+"F0.wireOp",EDGE,"E6.0.2.13"),sQuery(id+"F0.wireOp",EDGE,"E6.0.2.14"),sQuery(id+"F0.wireOp",EDGE,"E6.0.2.17"),sQuery(id+"F0.wireOp",EDGE,"E6.0.2.18"),sQuery(id+"F0.wireOp",EDGE,"E6.0.2.19"),sQuery(id+"F0.wireOp",EDGE,"E6.0.2.20"),sQuery(id+"F0.wireOp",EDGE,"E6.0.2.22"),sQuery(id+"F0.wireOp",EDGE,"E6.0.2.24"),sQuery(id+"F0.wireOp",EDGE,"E6.0.2.25"),sQuery(id+"F0.wireOp",EDGE,"E6.0.2.28"),sQuery(id+"F0.wireOp",EDGE,"E6.0.2.29"),sQuery(id+"F0.wireOp",EDGE,"E6.0.2.30"),sQuery(id+"F0.wireOp",EDGE,"E6.0.2.33"),sQuery(id+"F0.wireOp",EDGE,"E6.0.2.34"),sQuery(id+"F0.wireOp",EDGE,"E6.0.2.35"),sQuery(id+"F0.wireOp",EDGE,"E6.0.2.36"),sQuery(id+"F0.wireOp",EDGE,"E6.0.2.39"),sQuery(id+"F0.wireOp",EDGE,"E6.0.2.41"),sQuery(id+"F0.wireOp",EDGE,"E6.0.2.42"),sQuery(id+"F0.wireOp",EDGE,"E6.0.2.44"),sQuery(id+"F0.wireOp",EDGE,"E6.0.2.46"),sQuery(id+"F0.wireOp",EDGE,"E6.0.2.55"),sQuery(id+"F0.wireOp",EDGE,"E6.0.2.57"),sQuery(id+"F0.wireOp",EDGE,"E6.0.2.58"),sQuery(id+"F0.wireOp",EDGE,"E6.0.2.59"),sQuery(id+"F0.wireOp",EDGE,"E6.0.2.60"),sQuery(id+"F0.wireOp",EDGE,"E6.0.2.61"),sQuery(id+"F0.wireOp",EDGE,"E6.0.2.62"),sQuery(id+"F0.wireOp",EDGE,"E6.0.2.63"),sQuery(id+"F0.wireOp",EDGE,"E6.0.2.65"),sQuery(id+"F0.wireOp",EDGE,"E6.0.2.66"),sQuery(id+"F0.wireOp",EDGE,"E6.0.2.67"),sQuery(id+"F0.wireOp",EDGE,"E6.0.2.68"),sQuery(id+"F0.wireOp",EDGE,"E6.0.2.69"),sQuery(id+"F0.wireOp",EDGE,"E6.0.2.71"),sQuery(id+"F0.wireOp",EDGE,"E6.0.2.72"),sQuery(id+"F0.wireOp",EDGE,"E6.0.2.73"),sQuery(id+"F0.wireOp",EDGE,"E6.0.2.74"),sQuery(id+"F0.wireOp",EDGE,"E6.0.2.75"),sQuery(id+"F0.wireOp",EDGE,"E6.0.2.76"),sQuery(id+"F0.wireOp",EDGE,"E6.0.2.77"),sQuery(id+"F0.wireOp",EDGE,"E6.0.2.78"),sQuery(id+"F0.wireOp",EDGE,"E6.0.2.79"),sQuery(id+"F0.wireOp",EDGE,"E6.0.2.80"),sQuery(id+"F0.wireOp",EDGE,"E6.0.2.81"),sQuery(id+"F0.wireOp",EDGE,"E6.0.2.82"),sQuery(id+"F0.wireOp",EDGE,"E6.0.2.83"),sQuery(id+"F0.wireOp",EDGE,"E6.0.2.84"),sQuery(id+"F0.wireOp",EDGE,"E6.0.2.85"),sQuery(id+"F0.wireOp",EDGE,"E6.0.2.86"),sQuery(id+"F0.wireOp",EDGE,"E6.0.2.89"),sQuery(id+"F0.wireOp",EDGE,"E6.0.2.90"),sQuery(id+"F0.wireOp",EDGE,"E6.0.2.91"),sQuery(id+"F0.wireOp",EDGE,"E6.0.2.92"),sQuery(id+"F0.wireOp",EDGE,"E6.0.2.93"),sQuery(id+"F0.wireOp",EDGE,"E6.0.2.94"),sQuery(id+"F0.wireOp",EDGE,"E6.0.2.96"),sQuery(id+"F0.wireOp",EDGE,"E6.0.2.97"),sQuery(id+"F0.wireOp",EDGE,"E6.0.2.98"),sQuery(id+"F0.wireOp",EDGE,"E6.0.2.99"),sQuery(id+"F0.wireOp",EDGE,"E6.0.2.100"),sQuery(id+"F0.wireOp",EDGE,"E6.0.2.101"),sQuery(id+"F0.wireOp",EDGE,"E6.0.2.102"),sQuery(id+"F0.wireOp",EDGE,"E6.0.2.103"),sQuery(id+"F0.wireOp",EDGE,"E6.0.2.104"),sQuery(id+"F0.wireOp",EDGE,"E6.0.2.105"),sQuery(id+"F0.wireOp",EDGE,"E6.0.2.106"),sQuery(id+"F0.wireOp",EDGE,"E6.0.2.107"),sQuery(id+"F0.wireOp",EDGE,"E6.0.2.108"),sQuery(id+"F0.wireOp",EDGE,"E6.0.2.109"),sQuery(id+"F0.wireOp",EDGE,"E6.0.2.110"),sQuery(id+"F0.wireOp",EDGE,"E6.0.2.113"),sQuery(id+"F0.wireOp",EDGE,"E6.0.2.114"),sQuery(id+"F0.wireOp",EDGE,"E6.0.2.115"),sQuery(id+"F0.wireOp",EDGE,"E6.0.2.116"),sQuery(id+"F0.wireOp",EDGE,"E6.0.2.117"),sQuery(id+"F0.wireOp",EDGE,"E6.0.2.118"),sQuery(id+"F0.wireOp",EDGE,"E6.0.2.119"),sQuery(id+"F0.wireOp",EDGE,"E6.0.2.120"),sQuery(id+"F0.wireOp",EDGE,"E7"),sQuery(id+"F0.wireOp",EDGE,"E8"),sQuery(id+"F0.wireOp",EDGE,"E9"),sQuery(id+"F0.wireOp",EDGE,"E13.bottom"),sQuery(id+"F0.wireOp",EDGE,"E13.top"),sQuery(id+"F0.wireOp",EDGE,"E13.left"),sQuery(id+"F0.wireOp",EDGE,"E13.right"),sQuery(id+"F0.wireOp",EDGE,"E14.filletArc"),sQuery(id+"F0.wireOp",EDGE,"E15.filletArc"),sQuery(id+"F0.wireOp",EDGE,"E16.filletArc"),sQuery(id+"F0.wireOp",EDGE,"E17.filletArc"),sQuery(id+"F0.wireOp",EDGE,"E19.bottom"),sQuery(id+"F0.wireOp",EDGE,"E19.top"),sQuery(id+"F0.wireOp",EDGE,"E19.left"),sQuery(id+"F0.wireOp",EDGE,"E19.right"),sQuery(id+"F0.wireOp",EDGE,"E20"),sQuery(id+"F0.wireOp",EDGE,"E21.filletArc"),sQuery(id+"F0.wireOp",EDGE,"E22.filletArc"),sQuery(id+"F0.wireOp",EDGE,"E23.filletArc"),sQuery(id+"F0.wireOp",EDGE,"E24.filletArc"),sQuery(id+"F0.wireOp",EDGE,"E26.bottom"),sQuery(id+"F0.wireOp",EDGE,"E26.top"),sQuery(id+"F0.wireOp",EDGE,"E26.left"),sQuery(id+"F0.wireOp",EDGE,"E26.right"),sQuery(id+"F0.wireOp",EDGE,"E27.filletArc"),sQuery(id+"F0.wireOp",EDGE,"E28.filletArc"),sQuery(id+"F0.wireOp",EDGE,"E29.filletArc"),sQuery(id+"F0.wireOp",EDGE,"E30.filletArc"),sQuery(id+"F0.wireOp",EDGE,"E31.MirrorCS"),sQuery(id+"F0.wireOp",EDGE,"E32.MirrorCS"),sQuery(id+"F0.wireOp",EDGE,"E33.MirrorCS"),sQuery(id+"F0.wireOp",EDGE,"E34.MirrorCS"),sQuery(id+"F0.wireOp",EDGE,"E35.MirrorCS"),sQuery(id+"F0.wireOp",EDGE,"E36.MirrorCS"),sQuery(id+"F0.wireOp",EDGE,"E37.MirrorCS"),sQuery(id+"F0.wireOp",EDGE,"E38.MirrorCS"),sQuery(id+"F0.wireOp",EDGE,"E39.MirrorCS"),sQuery(id+"F0.wireOp",EDGE,"E44.MirrorCS"),sQuery(id+"F0.wireOp",EDGE,"E46.MirrorCS"),sQuery(id+"F0.wireOp",EDGE,"E47.MirrorCS"),sQuery(id+"F0.wireOp",EDGE,"E48.MirrorCS"),sQuery(id+"F0.wireOp",EDGE,"E49.MirrorCS"),sQuery(id+"F0.wireOp",EDGE,"E53.MirrorCS"),sQuery(id+"F0.wireOp",EDGE,"E54.MirrorCS"),sQuery(id+"F0.wireOp",EDGE,"E57.MirrorCS"),sQuery(id+"F0.wireOp",EDGE,"E60.bottom"),sQuery(id+"F0.wireOp",EDGE,"E60.top"),sQuery(id+"F0.wireOp",EDGE,"E60.left"),sQuery(id+"F0.wireOp",EDGE,"E60.right"),sQuery(id+"F0.wireOp",EDGE,"E62.filletArc"),sQuery(id+"F0.wireOp",EDGE,"E63.filletArc"),sQuery(id+"F0.wireOp",EDGE,"E64.filletArc"),sQuery(id+"F0.wireOp",EDGE,"E65.filletArc")])],"isStart":true});
            extrude(context, id + "F3", {"entities" : qUnion([Q0]), "operationType" : NewBodyOperationType.ADD, "endBound" : BoundingType.UP_TO_SURFACE, "oppositeDirection" : true, "endBoundEntityFace" : qUnion([Q1]), "depth" : 25 * mm});
        }
    });
